FCSTD DOCUMENT  (FreeCAD 1.0R39109 (Git))
Label: AluminumProfiles
License: All rights reserved
LicenseURL: https://en.wikipedia.org/wiki/All_rights_reserved
objects: Sketcher::SketchObject×4
note: 8 computed .brp shape members not serialized (recipe doc carries the construction recipe); baked Part::Feature solids carry a one-line shape summary decoded from their .brp

FEATURE [Sketcher::SketchObject] Sketch  label="2020-4"
  ArcFitTolerance = 1e-06
  FullyConstrained = false
  MakeInternals = false
  sketch-geometry (93):
    g0: LineSegment StartX=7.06065 StartY=6 StartZ=0 EndX=4 EndY=2.93934 EndZ=0
    g1: LineSegment StartX=4 StartY=2.93934 StartZ=0 EndX=4 EndY=2.5 EndZ=0
    g2: LineSegment StartX=4 StartY=2.5 StartZ=0 EndX=3.75098 EndY=1.21889 EndZ=0
    g3: LineSegment StartX=3.75098 StartY=1.21889 StartZ=0 EndX=3.93301 EndY=0.90359 EndZ=0
    g4: ArcOfCircle CenterX=3.5 CenterY=0.65359 CenterZ=0 NormalX=0 NormalY=0 NormalZ=1 AngleXU=0.523601 Radius=0.499998 StartAngle=5.23598 EndAngle=6.28319
    g5: LineSegment StartX=3.93301 StartY=0.40359 StartZ=0 EndX=3.7 EndY=-1e-16 EndZ=0
    g6: LineSegment StartX=3.7 StartY=-1e-16 StartZ=0 EndX=3.93301 EndY=-0.403589 EndZ=0
    g7: ArcOfCircle CenterX=3.5 CenterY=-0.653588 CenterZ=0 NormalX=0 NormalY=0 NormalZ=1 AngleXU=0.523603 Radius=0.499996 StartAngle=5.75958 EndAngle=6.28319
    g8: LineSegment StartX=4 StartY=-0.653589 StartZ=0 EndX=4 EndY=-2.93935 EndZ=0
    g9: LineSegment StartX=4 StartY=-2.93935 StartZ=0 EndX=7.06066 EndY=-6 EndZ=0
    g10: LineSegment StartX=7.06066 StartY=-6 StartZ=0 EndX=8 EndY=-6 EndZ=0
    g11: LineSegment StartX=8 StartY=-6 StartZ=0 EndX=8 EndY=-3.3 EndZ=0
    g12: ArcOfCircle CenterX=8.3 CenterY=-3.3 CenterZ=0 NormalX=0 NormalY=0 NormalZ=1 AngleXU=3.14159 Radius=0.3 StartAngle=4.71239 EndAngle=6.28319
    g13: LineSegment StartX=8.3 StartY=-3 StartZ=0 EndX=9.7 EndY=-3 EndZ=0
    g14: ArcOfCircle CenterX=9.7 CenterY=-3.3 CenterZ=0 NormalX=0 NormalY=0 NormalZ=1 AngleXU=1.5708 Radius=0.3 StartAngle=4.71239 EndAngle=6.28319
    g15: LineSegment StartX=10 StartY=-3.3 StartZ=0 EndX=10 EndY=-9 EndZ=0
    g16: ArcOfCircle CenterX=9 CenterY=-9 CenterZ=0 NormalX=0 NormalY=0 NormalZ=1 AngleXU=3.91e-14 Radius=1 StartAngle=4.71239 EndAngle=6.28319
    g17: LineSegment StartX=9 StartY=-10 StartZ=0 EndX=3.3 EndY=-10 EndZ=0
    g18: ArcOfCircle CenterX=3.3 CenterY=-9.7 CenterZ=0 NormalX=0 NormalY=0 NormalZ=1 AngleXU=-1.5708 Radius=0.3 StartAngle=4.71239 EndAngle=6.28319
    g19: LineSegment StartX=3 StartY=-9.7 StartZ=0 EndX=3 EndY=-8.3 EndZ=0
    g20: ArcOfCircle CenterX=3.3 CenterY=-8.3 CenterZ=0 NormalX=0 NormalY=0 NormalZ=1 AngleXU=3.14159 Radius=0.3 StartAngle=4.71239 EndAngle=6.28319
    g21: LineSegment StartX=3.3 StartY=-8 StartZ=0 EndX=6 EndY=-8 EndZ=0
    g22: LineSegment StartX=6 StartY=-8 StartZ=0 EndX=5.99999 EndY=-7.06066 EndZ=0
    g23: LineSegment StartX=5.99999 StartY=-7.06066 StartZ=0 EndX=2.93932 EndY=-4 EndZ=0
    g24: LineSegment StartX=2.93932 StartY=-4 StartZ=0 EndX=2.5 EndY=-4 EndZ=0
    g25: LineSegment StartX=2.5 StartY=-4 StartZ=0 EndX=1.21889 EndY=-3.75098 EndZ=0
    g26: LineSegment StartX=1.21889 StartY=-3.75098 StartZ=0 EndX=0.90359 EndY=-3.93301 EndZ=0
    g27: ArcOfCircle CenterX=0.65359 CenterY=-3.5 CenterZ=0 NormalX=0 NormalY=0 NormalZ=1 AngleXU=-1.0472 Radius=0.500001 StartAngle=5.23599 EndAngle=6.28319
    g28: LineSegment StartX=0.40359 StartY=-3.93301 StartZ=0 EndX=-1e-16 EndY=-3.7 EndZ=0
    g29: LineSegment StartX=-1e-16 StartY=-3.7 StartZ=0 EndX=-0.403589 EndY=-3.93301 EndZ=0
    g30: ArcOfCircle CenterX=-0.653589 CenterY=-3.5 CenterZ=0 NormalX=0 NormalY=0 NormalZ=1 AngleXU=-1.0472 Radius=0.500002 StartAngle=5.75959 EndAngle=6.28319
    g31: LineSegment StartX=-0.653589 StartY=-4 StartZ=0 EndX=-2.93935 EndY=-4 EndZ=0
    g32: LineSegment StartX=-2.93935 StartY=-4 StartZ=0 EndX=-6 EndY=-7.06066 EndZ=0
    g33: LineSegment StartX=-6 StartY=-7.06066 StartZ=0 EndX=-6 EndY=-8 EndZ=0
    g34: LineSegment StartX=-6 StartY=-8 StartZ=0 EndX=-3.3 EndY=-8 EndZ=0
    g35: ArcOfCircle CenterX=-3.3 CenterY=-8.3 CenterZ=0 NormalX=0 NormalY=0 NormalZ=1 AngleXU=1.5708 Radius=0.3 StartAngle=4.71239 EndAngle=6.28319
    g36: LineSegment StartX=-3 StartY=-8.3 StartZ=0 EndX=-3 EndY=-9.7 EndZ=0
    g37: ArcOfCircle CenterX=-3.3 CenterY=-9.7 CenterZ=0 NormalX=0 NormalY=0 NormalZ=1 AngleXU=1.82496e-07 Radius=0.3 StartAngle=4.71239 EndAngle=6.28319
    g38: ArcOfCircle CenterX=-9 CenterY=-9 CenterZ=0 NormalX=0 NormalY=0 NormalZ=1 AngleXU=-1.5708 Radius=1 StartAngle=4.71239 EndAngle=6.28319
    g39: LineSegment StartX=-10 StartY=-9 StartZ=0 EndX=-10 EndY=-3.3 EndZ=0
    g40: ArcOfCircle CenterX=-9.7 CenterY=-3.3 CenterZ=0 NormalX=0 NormalY=0 NormalZ=1 AngleXU=-3.14159 Radius=0.3 StartAngle=4.71239 EndAngle=6.28319
    g41: LineSegment StartX=-9.7 StartY=-3 StartZ=0 EndX=-8.3 EndY=-3 EndZ=0
    g42: ArcOfCircle CenterX=-8.3 CenterY=-3.3 CenterZ=0 NormalX=0 NormalY=0 NormalZ=1 AngleXU=1.5708 Radius=0.3 StartAngle=4.71239 EndAngle=6.28319
    g43: LineSegment StartX=-8 StartY=-3.3 StartZ=0 EndX=-8 EndY=-6 EndZ=0
    g44: LineSegment StartX=-8 StartY=-6 StartZ=0 EndX=-7.06067 EndY=-6 EndZ=0
    g45: LineSegment StartX=-7.06067 StartY=-6 StartZ=0 EndX=-4 EndY=-2.93934 EndZ=0
    g46: LineSegment StartX=-4 StartY=-2.93934 StartZ=0 EndX=-4 EndY=-2.5 EndZ=0
    g47: LineSegment StartX=-4 StartY=-2.5 StartZ=0 EndX=-3.75098 EndY=-1.21889 EndZ=0
    g48: LineSegment StartX=-3.75098 StartY=-1.21889 StartZ=0 EndX=-3.93301 EndY=-0.903589 EndZ=0
    g49: ArcOfCircle CenterX=-3.5 CenterY=-0.653589 CenterZ=0 NormalX=0 NormalY=0 NormalZ=1 AngleXU=-2.61799 Radius=0.499998 StartAngle=5.23598 EndAngle=6.28319
    g50: LineSegment StartX=-3.93301 StartY=-0.403589 StartZ=0 EndX=-3.7 EndY=0 EndZ=0
    g51: LineSegment StartX=-3.7 StartY=0 StartZ=0 EndX=-3.93301 EndY=0.40359 EndZ=0
    g52: ArcOfCircle CenterX=-3.5 CenterY=0.653589 CenterZ=0 NormalX=0 NormalY=0 NormalZ=1 AngleXU=-2.61799 Radius=0.499996 StartAngle=5.75958 EndAngle=6.28319
    g53: LineSegment StartX=-4 StartY=0.65359 StartZ=0 EndX=-4 EndY=2.93933 EndZ=0
    g54: LineSegment StartX=-4 StartY=2.93933 StartZ=0 EndX=-7.06067 EndY=6 EndZ=0
    g55: LineSegment StartX=-7.06067 StartY=6 StartZ=0 EndX=-8 EndY=6 EndZ=0
    g56: LineSegment StartX=-8 StartY=6 StartZ=0 EndX=-8 EndY=3.3 EndZ=0
    g57: ArcOfCircle CenterX=-8.3 CenterY=3.3 CenterZ=0 NormalX=0 NormalY=0 NormalZ=1 AngleXU=4.74e-14 Radius=0.3 StartAngle=4.71239 EndAngle=6.28319
    g58: LineSegment StartX=-8.3 StartY=3 StartZ=0 EndX=-9.7 EndY=3 EndZ=0
    g59: ArcOfCircle CenterX=-9.7 CenterY=3.3 CenterZ=0 NormalX=0 NormalY=0 NormalZ=1 AngleXU=-1.5708 Radius=0.3 StartAngle=4.71239 EndAngle=6.28319
    g60: LineSegment StartX=-10 StartY=3.3 StartZ=0 EndX=-10 EndY=9 EndZ=0
    g61: ArcOfCircle CenterX=-9 CenterY=9 CenterZ=0 NormalX=0 NormalY=0 NormalZ=1 AngleXU=3.14159 Radius=1 StartAngle=4.71239 EndAngle=6.28319
    g62: LineSegment StartX=-9 StartY=10 StartZ=0 EndX=-3.3 EndY=10 EndZ=0
    g63: ArcOfCircle CenterX=-3.3 CenterY=9.7 CenterZ=0 NormalX=0 NormalY=0 NormalZ=1 AngleXU=1.5708 Radius=0.3 StartAngle=4.71239 EndAngle=6.28319
    g64: LineSegment StartX=-3 StartY=9.7 StartZ=0 EndX=-3 EndY=8.3 EndZ=0
    g65: ArcOfCircle CenterX=-3.3 CenterY=8.3 CenterZ=0 NormalX=0 NormalY=0 NormalZ=1 AngleXU=2.96e-14 Radius=0.3 StartAngle=4.71239 EndAngle=6.28319
    g66: LineSegment StartX=-3.3 StartY=8 StartZ=0 EndX=-6 EndY=8 EndZ=0
    g67: LineSegment StartX=-6 StartY=8 StartZ=0 EndX=-6 EndY=7.06064 EndZ=0
    g68: LineSegment StartX=-6 StartY=7.06064 StartZ=0 EndX=-2.93936 EndY=4 EndZ=0
    g69: LineSegment StartX=-2.93936 StartY=4 StartZ=0 EndX=-2.5 EndY=4 EndZ=0
    g70: LineSegment StartX=-2.5 StartY=4 StartZ=0 EndX=-1.21888 EndY=3.75098 EndZ=0
    g71: LineSegment StartX=-1.21888 StartY=3.75098 StartZ=0 EndX=-0.903589 EndY=3.93301 EndZ=0
    g72: ArcOfCircle CenterX=-0.653589 CenterY=3.5 CenterZ=0 NormalX=0 NormalY=0 NormalZ=1 AngleXU=2.09439 Radius=0.500001 StartAngle=5.23599 EndAngle=6.28319
    g73: LineSegment StartX=-0.403589 StartY=3.93301 StartZ=0 EndX=0 EndY=3.7 EndZ=0
    g74: LineSegment StartX=0 StartY=3.7 StartZ=0 EndX=0.40359 EndY=3.93301 EndZ=0
    g75: ArcOfCircle CenterX=0.65359 CenterY=3.5 CenterZ=0 NormalX=0 NormalY=0 NormalZ=1 AngleXU=2.09439 Radius=0.500002 StartAngle=5.75959 EndAngle=6.28319
    g76: LineSegment StartX=0.65359 StartY=4 StartZ=0 EndX=2.93933 EndY=4 EndZ=0
    g77: LineSegment StartX=2.93933 StartY=4 StartZ=0 EndX=6 EndY=7.06067 EndZ=0
    g78: LineSegment StartX=6 StartY=7.06067 StartZ=0 EndX=6 EndY=8 EndZ=0
    g79: LineSegment StartX=6 StartY=8 StartZ=0 EndX=3.3 EndY=8 EndZ=0
    g80: ArcOfCircle CenterX=3.3 CenterY=8.3 CenterZ=0 NormalX=0 NormalY=0 NormalZ=1 AngleXU=-1.5708 Radius=0.3 StartAngle=4.71239 EndAngle=6.28319
    g81: LineSegment StartX=3 StartY=8.3 StartZ=0 EndX=3 EndY=9.7 EndZ=0
    g82: ArcOfCircle CenterX=3.3 CenterY=9.7 CenterZ=0 NormalX=0 NormalY=0 NormalZ=1 AngleXU=-3.14159 Radius=0.3 StartAngle=4.71239 EndAngle=6.28319
    g83: LineSegment StartX=3.3 StartY=10 StartZ=0 EndX=9 EndY=10 EndZ=0
    g84: ArcOfCircle CenterX=9 CenterY=9 CenterZ=0 NormalX=0 NormalY=0 NormalZ=1 AngleXU=1.5708 Radius=1 StartAngle=4.71239 EndAngle=6.28319
    g85: LineSegment StartX=10 StartY=9 StartZ=0 EndX=10 EndY=3.3 EndZ=0
    g86: ArcOfCircle CenterX=9.7 CenterY=3.3 CenterZ=0 NormalX=0 NormalY=0 NormalZ=1 AngleXU=9.91623e-08 Radius=0.3 StartAngle=4.71239 EndAngle=6.28319
    g87: LineSegment StartX=9.7 StartY=3 StartZ=0 EndX=8.3 EndY=3 EndZ=0
    g88: ArcOfCircle CenterX=8.3 CenterY=3.3 CenterZ=0 NormalX=0 NormalY=0 NormalZ=1 AngleXU=-1.5708 Radius=0.3 StartAngle=4.71239 EndAngle=6.28319
    g89: LineSegment StartX=8 StartY=3.3 StartZ=0 EndX=8 EndY=6 EndZ=0
    g90: LineSegment StartX=8 StartY=6 StartZ=0 EndX=7.06065 EndY=6 EndZ=0
    g91: Circle CenterX=0 CenterY=-2.84e-14 CenterZ=0 NormalX=0 NormalY=0 NormalZ=-1 AngleXU=0 Radius=2.1
    g92: LineSegment StartX=-9 StartY=-10 StartZ=0 EndX=-3.3 EndY=-10 EndZ=0
  constraints (93):
    c: Coincident(g92,g38)
    c: Coincident(g92,g37)
    c: Horizontal(g92)
    c: Coincident(g38,g39)
    c: Coincident(g39,g40)
    c: Coincident(g59,g60)
    c: Coincident(g60,g61)
    c: Coincident(g40,g41)
    c: Coincident(g58,g59)
    c: Coincident(g61,g62)
    c: Coincident(g41,g42)
    c: Coincident(g57,g58)
    c: Coincident(g43,g44)
    c: Coincident(g42,g43)
    c: Coincident(g56,g57)
    c: Coincident(g55,g56)
    c: Coincident(g44,g45)
    c: Coincident(g54,g55)
    c: Coincident(g33,g34)
    c: Coincident(g32,g33)
    c: Coincident(g67,g68)
    c: Coincident(g66,g67)
    c: Coincident(g45,g46)
    c: Coincident(g46,g47)
    c: Coincident(g52,g53)
    c: Coincident(g53,g54)
    c: Coincident(g48,g49)
    c: Coincident(g49,g50)
    c: Coincident(g51,g52)
    c: Coincident(g47,g48)
    c: Coincident(g50,g51)
    c: Coincident(g34,g35)
    c: Coincident(g65,g66)
    c: Coincident(g62,g63)
    c: Coincident(g36,g37)
    c: Coincident(g35,g36)
    c: Coincident(g64,g65)
    c: Coincident(g63,g64)
    c: Coincident(g31,g32)
    c: Coincident(g68,g69)
    c: Coincident(g69,g70)
    c: Coincident(g70,g71)
    c: Coincident(g71,g72)
    c: Coincident(g30,g31)
    c: Coincident(g29,g30)
    c: Coincident(g72,g73)
    c: Coincident(g28,g29)
    c: Coincident(g73,g74)
    c: Coincident(g27,g28)
    c: Coincident(g74,g75)
    c: Coincident(g75,g76)
    c: Coincident(g26,g27)
    c: Coincident(g25,g26)
    c: Coincident(g24,g25)
    c: Coincident(g23,g24)
    c: Coincident(g76,g77)
    c: Coincident(g18,g19)
    c: Coincident(g19,g20)
    c: Coincident(g80,g81)
    c: Coincident(g81,g82)
    c: Coincident(g17,g18)
    c: Coincident(g20,g21)
    c: Coincident(g79,g80)
    c: Coincident(g82,g83)
    c: Coincident(g5,g6)
    c: Coincident(g2,g3)
    c: Coincident(g6,g7)
    c: Coincident(g4,g5)
    c: Coincident(g3,g4)
    c: Coincident(g8,g9)
    c: Coincident(g7,g8)
    c: Coincident(g1,g2)
    c: Coincident(g0,g1)
    c: Coincident(g21,g22)
    c: Coincident(g22,g23)
    c: Coincident(g77,g78)
    c: Coincident(g78,g79)
    c: Coincident(g9,g10)
    c: Coincident(g0,g90)
    c: Coincident(g10,g11)
    c: Coincident(g11,g12)
    c: Coincident(g88,g89)
    c: Coincident(g89,g90)
    c: Coincident(g12,g13)
    c: Coincident(g87,g88)
    c: Coincident(g16,g17)
    c: Coincident(g83,g84)
    c: Coincident(g13,g14)
    c: Coincident(g86,g87)
    c: Coincident(g15,g16)
    c: Coincident(g14,g15)
    c: Coincident(g85,g86)
    c: Coincident(g84,g85)
FEATURE [Sketcher::SketchObject] Sketch001  label="2080-10"
  ArcFitTolerance = 1e-06
  FullyConstrained = false
  MakeInternals = false
  sketch-geometry (287):
    g0: LineSegment StartX=-39 StartY=-10 StartZ=0 EndX=-33.3 EndY=-10 EndZ=0
    g1: ArcOfCircle CenterX=-33.3 CenterY=-9.7 CenterZ=0 NormalX=0 NormalY=0 NormalZ=1 AngleXU=0 Radius=0.3 StartAngle=4.71239 EndAngle=6.28319
    g2: LineSegment StartX=-33 StartY=-9.7 StartZ=0 EndX=-33 EndY=-8.3 EndZ=0
    g3: ArcOfCircle CenterX=-33.3 CenterY=-8.3 CenterZ=0 NormalX=0 NormalY=0 NormalZ=1 AngleXU=0 Radius=0.3 StartAngle=0 EndAngle=1.5708
    g4: LineSegment StartX=-33.3 StartY=-8 StartZ=0 EndX=-36 EndY=-8 EndZ=0
    g5: LineSegment StartX=-36 StartY=-8 StartZ=0 EndX=-36 EndY=-7.06065 EndZ=0
    g6: LineSegment StartX=-36 StartY=-7.06065 StartZ=0 EndX=-32.9394 EndY=-4 EndZ=0
    g7: LineSegment StartX=-32.9394 StartY=-4 StartZ=0 EndX=-30.6536 EndY=-4 EndZ=0
    g8: ArcOfCircle CenterX=-30.6536 CenterY=-3.5 CenterZ=0 NormalX=0 NormalY=0 NormalZ=1 AngleXU=0 Radius=0.500002 StartAngle=4.71239 EndAngle=5.23599
    g9: LineSegment StartX=-30.4036 StartY=-3.93301 StartZ=0 EndX=-30 EndY=-3.7 EndZ=0
    g10: LineSegment StartX=-30 StartY=-3.7 StartZ=0 EndX=-29.5964 EndY=-3.93301 EndZ=0
    g11: ArcOfCircle CenterX=-29.3464 CenterY=-3.5 CenterZ=0 NormalX=0 NormalY=0 NormalZ=1 AngleXU=0 Radius=0.500001 StartAngle=4.18879 EndAngle=5.23599
    g12: LineSegment StartX=-29.0964 StartY=-3.93301 StartZ=0 EndX=-28.7811 EndY=-3.75098 EndZ=0
    g13: LineSegment StartX=-28.7811 StartY=-3.75098 StartZ=0 EndX=-27.5 EndY=-4 EndZ=0
    g14: LineSegment StartX=-27.5 StartY=-4 StartZ=0 EndX=-27.0607 EndY=-4 EndZ=0
    g15: LineSegment StartX=-27.0607 StartY=-4 StartZ=0 EndX=-24 EndY=-7.06068 EndZ=0
    g16: LineSegment StartX=-24 StartY=-7.06068 StartZ=0 EndX=-24 EndY=-8 EndZ=0
    g17: LineSegment StartX=-24 StartY=-8 StartZ=0 EndX=-26.7 EndY=-8 EndZ=0
    g18: ArcOfCircle CenterX=-26.7 CenterY=-8.3 CenterZ=0 NormalX=0 NormalY=0 NormalZ=1 AngleXU=0 Radius=0.3 StartAngle=1.5708 EndAngle=3.14159
    g19: LineSegment StartX=-27 StartY=-8.3 StartZ=0 EndX=-27 EndY=-9.7 EndZ=0
    g20: ArcOfCircle CenterX=-26.7 CenterY=-9.7 CenterZ=0 NormalX=0 NormalY=0 NormalZ=1 AngleXU=0 Radius=0.3 StartAngle=3.14159 EndAngle=4.71239
    g21: LineSegment StartX=-26.7 StartY=-10 StartZ=0 EndX=-13.3 EndY=-10 EndZ=0
    g22: ArcOfCircle CenterX=-13.3 CenterY=-9.7 CenterZ=0 NormalX=0 NormalY=0 NormalZ=1 AngleXU=0 Radius=0.3 StartAngle=4.71239 EndAngle=6.28319
    g23: LineSegment StartX=-13 StartY=-9.7 StartZ=0 EndX=-13 EndY=-8.3 EndZ=0
    g24: ArcOfCircle CenterX=-13.3 CenterY=-8.3 CenterZ=0 NormalX=0 NormalY=0 NormalZ=1 AngleXU=0 Radius=0.3 StartAngle=0 EndAngle=1.5708
    g25: LineSegment StartX=-13.3 StartY=-8 StartZ=0 EndX=-16 EndY=-8 EndZ=0
    g26: LineSegment StartX=-16 StartY=-8 StartZ=0 EndX=-16 EndY=-7.06065 EndZ=0
    g27: LineSegment StartX=-16 StartY=-7.06065 StartZ=0 EndX=-12.9394 EndY=-4 EndZ=0
    g28: LineSegment StartX=-12.9394 StartY=-4 StartZ=0 EndX=-10.6536 EndY=-4 EndZ=0
    g29: ArcOfCircle CenterX=-10.6536 CenterY=-3.5 CenterZ=0 NormalX=0 NormalY=0 NormalZ=1 AngleXU=0 Radius=0.500002 StartAngle=4.71239 EndAngle=5.23599
    g30: LineSegment StartX=-10.4036 StartY=-3.93301 StartZ=0 EndX=-10 EndY=-3.7 EndZ=0
    g31: LineSegment StartX=-10 StartY=-3.7 StartZ=0 EndX=-9.59641 EndY=-3.93301 EndZ=0
    g32: ArcOfCircle CenterX=-9.34641 CenterY=-3.5 CenterZ=0 NormalX=0 NormalY=0 NormalZ=1 AngleXU=0 Radius=0.500001 StartAngle=4.18879 EndAngle=5.23599
    g33: LineSegment StartX=-9.09641 StartY=-3.93301 StartZ=0 EndX=-8.78111 EndY=-3.75098 EndZ=0
    g34: LineSegment StartX=-8.78111 StartY=-3.75098 StartZ=0 EndX=-7.5 EndY=-4 EndZ=0
    g35: LineSegment StartX=-7.5 StartY=-4 StartZ=0 EndX=-7.06067 EndY=-4 EndZ=0
    g36: LineSegment StartX=-7.06067 StartY=-4 StartZ=0 EndX=-4.00001 EndY=-7.06066 EndZ=0
    g37: LineSegment StartX=-4.00001 StartY=-7.06066 StartZ=0 EndX=-4.00001 EndY=-8 EndZ=0
    g38: LineSegment StartX=-4.00001 StartY=-8 StartZ=0 EndX=-6.70001 EndY=-8 EndZ=0
    g39: ArcOfCircle CenterX=-6.70001 CenterY=-8.3 CenterZ=0 NormalX=0 NormalY=0 NormalZ=1 AngleXU=0 Radius=0.3 StartAngle=1.5708 EndAngle=3.14159
    g40: LineSegment StartX=-7.00001 StartY=-8.3 StartZ=0 EndX=-7.00001 EndY=-9.7 EndZ=0
    g41: ArcOfCircle CenterX=-6.70001 CenterY=-9.7 CenterZ=0 NormalX=0 NormalY=0 NormalZ=1 AngleXU=0 Radius=0.3 StartAngle=3.14159 EndAngle=4.71239
    g42: LineSegment StartX=-6.70001 StartY=-10 StartZ=0 EndX=-1.3e-05 EndY=-10 EndZ=0
    g43: LineSegment StartX=-1.3e-05 StartY=-10 StartZ=0 EndX=6.69999 EndY=-10 EndZ=0
    g44: ArcOfCircle CenterX=6.69999 CenterY=-9.7 CenterZ=0 NormalX=0 NormalY=0 NormalZ=1 AngleXU=0 Radius=0.3 StartAngle=4.71239 EndAngle=6.28319
    g45: LineSegment StartX=6.99999 StartY=-9.7 StartZ=0 EndX=6.99999 EndY=-8.3 EndZ=0
    g46: ArcOfCircle CenterX=6.69999 CenterY=-8.3 CenterZ=0 NormalX=0 NormalY=0 NormalZ=1 AngleXU=0 Radius=0.3 StartAngle=0 EndAngle=1.5708
    g47: LineSegment StartX=6.69999 StartY=-8 StartZ=0 EndX=3.99999 EndY=-8 EndZ=0
    g48: LineSegment StartX=3.99999 StartY=-8 StartZ=0 EndX=3.99999 EndY=-7.06065 EndZ=0
    g49: LineSegment StartX=3.99999 StartY=-7.06065 StartZ=0 EndX=7.06064 EndY=-4 EndZ=0
    g50: LineSegment StartX=7.06064 StartY=-4 StartZ=0 EndX=9.34642 EndY=-4 EndZ=0
    g51: ArcOfCircle CenterX=9.34642 CenterY=-3.5 CenterZ=0 NormalX=0 NormalY=0 NormalZ=1 AngleXU=0 Radius=0.500002 StartAngle=4.71239 EndAngle=5.23599
    g52: LineSegment StartX=9.59642 StartY=-3.93301 StartZ=0 EndX=10 EndY=-3.7 EndZ=0
    g53: LineSegment StartX=10 StartY=-3.7 StartZ=0 EndX=10.4036 EndY=-3.93301 EndZ=0
    g54: ArcOfCircle CenterX=10.6536 CenterY=-3.5 CenterZ=0 NormalX=0 NormalY=0 NormalZ=1 AngleXU=0 Radius=0.500001 StartAngle=4.18879 EndAngle=5.23599
    g55: LineSegment StartX=10.9036 StartY=-3.93301 StartZ=0 EndX=11.2189 EndY=-3.75098 EndZ=0
    g56: LineSegment StartX=11.2189 StartY=-3.75098 StartZ=0 EndX=12.5 EndY=-4 EndZ=0
    g57: LineSegment StartX=12.5 StartY=-4 StartZ=0 EndX=12.9393 EndY=-4 EndZ=0
    g58: LineSegment StartX=12.9393 StartY=-4 StartZ=0 EndX=16 EndY=-7.06066 EndZ=0
    g59: LineSegment StartX=16 StartY=-7.06066 StartZ=0 EndX=16 EndY=-8 EndZ=0
    g60: LineSegment StartX=16 StartY=-8 StartZ=0 EndX=13.3 EndY=-8 EndZ=0
    g61: ArcOfCircle CenterX=13.3 CenterY=-8.3 CenterZ=0 NormalX=0 NormalY=0 NormalZ=1 AngleXU=0 Radius=0.3 StartAngle=1.5708 EndAngle=3.14159
    g62: LineSegment StartX=13 StartY=-8.3 StartZ=0 EndX=13 EndY=-9.7 EndZ=0
    g63: ArcOfCircle CenterX=13.3 CenterY=-9.7 CenterZ=0 NormalX=0 NormalY=0 NormalZ=1 AngleXU=0 Radius=0.3 StartAngle=3.14159 EndAngle=4.71239
    g64: LineSegment StartX=13.3 StartY=-10 StartZ=0 EndX=26.7 EndY=-10 EndZ=0
    g65: ArcOfCircle CenterX=26.7 CenterY=-9.7 CenterZ=0 NormalX=0 NormalY=0 NormalZ=1 AngleXU=0 Radius=0.3 StartAngle=4.71239 EndAngle=6.28319
    g66: LineSegment StartX=27 StartY=-9.7 StartZ=0 EndX=27 EndY=-8.3 EndZ=0
    g67: ArcOfCircle CenterX=26.7 CenterY=-8.3 CenterZ=0 NormalX=0 NormalY=0 NormalZ=1 AngleXU=0 Radius=0.3 StartAngle=0 EndAngle=1.5708
    g68: LineSegment StartX=26.7 StartY=-8 StartZ=0 EndX=24 EndY=-8 EndZ=0
    g69: LineSegment StartX=24 StartY=-8 StartZ=0 EndX=24 EndY=-7.06066 EndZ=0
    g70: LineSegment StartX=24 StartY=-7.06066 StartZ=0 EndX=27.0606 EndY=-4 EndZ=0
    g71: LineSegment StartX=27.0606 StartY=-4 StartZ=0 EndX=29.3464 EndY=-4 EndZ=0
    g72: ArcOfCircle CenterX=29.3464 CenterY=-3.5 CenterZ=0 NormalX=0 NormalY=0 NormalZ=1 AngleXU=0 Radius=0.500002 StartAngle=4.71239 EndAngle=5.23599
    g73: LineSegment StartX=29.5964 StartY=-3.93301 StartZ=0 EndX=30 EndY=-3.7 EndZ=0
    g74: LineSegment StartX=30 StartY=-3.7 StartZ=0 EndX=30.4036 EndY=-3.93301 EndZ=0
    g75: ArcOfCircle CenterX=30.6536 CenterY=-3.5 CenterZ=0 NormalX=0 NormalY=0 NormalZ=1 AngleXU=0 Radius=0.500001 StartAngle=4.18879 EndAngle=5.23599
    g76: LineSegment StartX=30.9036 StartY=-3.93301 StartZ=0 EndX=31.2189 EndY=-3.75098 EndZ=0
    g77: LineSegment StartX=31.2189 StartY=-3.75098 StartZ=0 EndX=32.5 EndY=-4 EndZ=0
    g78: LineSegment StartX=32.5 StartY=-4 StartZ=0 EndX=32.9393 EndY=-4 EndZ=0
    g79: LineSegment StartX=32.9393 StartY=-4 StartZ=0 EndX=36 EndY=-7.06064 EndZ=0
    g80: LineSegment StartX=36 StartY=-7.06064 StartZ=0 EndX=36 EndY=-8 EndZ=0
    g81: LineSegment StartX=36 StartY=-8 StartZ=0 EndX=33.3 EndY=-8 EndZ=0
    g82: ArcOfCircle CenterX=33.3 CenterY=-8.3 CenterZ=0 NormalX=0 NormalY=0 NormalZ=1 AngleXU=0 Radius=0.3 StartAngle=1.5708 EndAngle=3.14159
    g83: LineSegment StartX=33 StartY=-8.3 StartZ=0 EndX=33 EndY=-9.7 EndZ=0
    g84: ArcOfCircle CenterX=33.3 CenterY=-9.7 CenterZ=0 NormalX=0 NormalY=0 NormalZ=1 AngleXU=0 Radius=0.3 StartAngle=3.14159 EndAngle=4.71239
    g85: LineSegment StartX=33.3 StartY=-10 StartZ=0 EndX=39 EndY=-10 EndZ=0
    g86: ArcOfCircle CenterX=39 CenterY=-9 CenterZ=0 NormalX=0 NormalY=0 NormalZ=1 AngleXU=0 Radius=1 StartAngle=4.71239 EndAngle=6.28319
    g87: LineSegment StartX=40 StartY=-9 StartZ=0 EndX=40 EndY=-3.3 EndZ=0
    g88: ArcOfCircle CenterX=39.7 CenterY=-3.3 CenterZ=0 NormalX=0 NormalY=0 NormalZ=1 AngleXU=0 Radius=0.3 StartAngle=0 EndAngle=1.5708
    g89: LineSegment StartX=39.7 StartY=-3 StartZ=0 EndX=38.3 EndY=-3 EndZ=0
    g90: ArcOfCircle CenterX=38.3 CenterY=-3.3 CenterZ=0 NormalX=0 NormalY=0 NormalZ=1 AngleXU=0 Radius=0.3 StartAngle=1.5708 EndAngle=3.14159
    g91: LineSegment StartX=38 StartY=-3.3 StartZ=0 EndX=38 EndY=-6 EndZ=0
    g92: LineSegment StartX=38 StartY=-6 StartZ=0 EndX=37.0607 EndY=-6 EndZ=0
    g93: LineSegment StartX=37.0607 StartY=-6 StartZ=0 EndX=34 EndY=-2.93932 EndZ=0
    g94: LineSegment StartX=34 StartY=-2.93932 StartZ=0 EndX=34 EndY=-0.653589 EndZ=0
    g95: ArcOfCircle CenterX=33.5 CenterY=-0.653589 CenterZ=0 NormalX=0 NormalY=0 NormalZ=1 AngleXU=0 Radius=0.499996 StartAngle=6.28318 EndAngle=6.80679
    g96: LineSegment StartX=33.933 StartY=-0.403589 StartZ=0 EndX=33.7 EndY=0 EndZ=0
    g97: LineSegment StartX=33.7 StartY=0 StartZ=0 EndX=33.933 EndY=0.403589 EndZ=0
    g98: ArcOfCircle CenterX=33.5 CenterY=0.653589 CenterZ=0 NormalX=0 NormalY=0 NormalZ=1 AngleXU=0 Radius=0.499998 StartAngle=5.75958 EndAngle=6.80679
    g99: LineSegment StartX=33.933 StartY=0.903589 StartZ=0 EndX=33.751 EndY=1.21889 EndZ=0
    g100: LineSegment StartX=33.751 StartY=1.21889 StartZ=0 EndX=34 EndY=2.5 EndZ=0
    g101: LineSegment StartX=34 StartY=2.5 StartZ=0 EndX=34 EndY=2.93932 EndZ=0
    g102: LineSegment StartX=34 StartY=2.93932 StartZ=0 EndX=37.0607 EndY=6 EndZ=0
    g103: LineSegment StartX=37.0607 StartY=6 StartZ=0 EndX=38 EndY=6 EndZ=0
    g104: LineSegment StartX=38 StartY=6 StartZ=0 EndX=38 EndY=3.3 EndZ=0
    g105: ArcOfCircle CenterX=38.3 CenterY=3.3 CenterZ=0 NormalX=0 NormalY=0 NormalZ=1 AngleXU=0 Radius=0.3 StartAngle=3.14159 EndAngle=4.71239
    g106: LineSegment StartX=38.3 StartY=3 StartZ=0 EndX=39.7 EndY=3 EndZ=0
    g107: ArcOfCircle CenterX=39.7 CenterY=3.3 CenterZ=0 NormalX=0 NormalY=0 NormalZ=1 AngleXU=0 Radius=0.3 StartAngle=4.71239 EndAngle=6.28319
    g108: LineSegment StartX=40 StartY=3.3 StartZ=0 EndX=40 EndY=9 EndZ=0
    g109: ArcOfCircle CenterX=39 CenterY=9 CenterZ=0 NormalX=0 NormalY=0 NormalZ=1 AngleXU=0 Radius=1 StartAngle=6.28319 EndAngle=7.85398
    g110: LineSegment StartX=39 StartY=10 StartZ=0 EndX=33.3 EndY=10 EndZ=0
    g111: ArcOfCircle CenterX=33.3 CenterY=9.7 CenterZ=0 NormalX=0 NormalY=0 NormalZ=1 AngleXU=0 Radius=0.3 StartAngle=1.5708 EndAngle=3.14159
    g112: LineSegment StartX=33 StartY=9.7 StartZ=0 EndX=33 EndY=8.3 EndZ=0
    g113: ArcOfCircle CenterX=33.3 CenterY=8.3 CenterZ=0 NormalX=0 NormalY=0 NormalZ=1 AngleXU=0 Radius=0.3 StartAngle=3.14159 EndAngle=4.71239
    g114: LineSegment StartX=33.3 StartY=8 StartZ=0 EndX=36 EndY=8 EndZ=0
    g115: LineSegment StartX=36 StartY=8 StartZ=0 EndX=36 EndY=7.06064 EndZ=0
    g116: LineSegment StartX=36 StartY=7.06064 StartZ=0 EndX=32.9393 EndY=4 EndZ=0
    g117: LineSegment StartX=32.9393 StartY=4 StartZ=0 EndX=30.6536 EndY=4 EndZ=0
    g118: ArcOfCircle CenterX=30.6536 CenterY=3.5 CenterZ=0 NormalX=0 NormalY=0 NormalZ=1 AngleXU=0 Radius=0.500002 StartAngle=1.5708 EndAngle=2.09439
    g119: LineSegment StartX=30.4036 StartY=3.93301 StartZ=0 EndX=30 EndY=3.7 EndZ=0
    g120: LineSegment StartX=30 StartY=3.7 StartZ=0 EndX=29.5964 EndY=3.93301 EndZ=0
    g121: ArcOfCircle CenterX=29.3464 CenterY=3.5 CenterZ=0 NormalX=0 NormalY=0 NormalZ=1 AngleXU=0 Radius=0.500001 StartAngle=1.0472 EndAngle=2.09439
    g122: LineSegment StartX=29.0964 StartY=3.93301 StartZ=0 EndX=28.7811 EndY=3.75098 EndZ=0
    g123: LineSegment StartX=28.7811 StartY=3.75098 StartZ=0 EndX=27.5 EndY=4 EndZ=0
    g124: LineSegment StartX=27.5 StartY=4 StartZ=0 EndX=27.0607 EndY=4 EndZ=0
    g125: LineSegment StartX=27.0607 StartY=4 StartZ=0 EndX=24 EndY=7.06067 EndZ=0
    g126: LineSegment StartX=24 StartY=7.06067 StartZ=0 EndX=24 EndY=8 EndZ=0
    g127: LineSegment StartX=24 StartY=8 StartZ=0 EndX=26.7 EndY=8 EndZ=0
    g128: ArcOfCircle CenterX=26.7 CenterY=8.3 CenterZ=0 NormalX=0 NormalY=0 NormalZ=1 AngleXU=0 Radius=0.3 StartAngle=4.71239 EndAngle=6.28319
    g129: LineSegment StartX=27 StartY=8.3 StartZ=0 EndX=27 EndY=9.7 EndZ=0
    g130: ArcOfCircle CenterX=26.7 CenterY=9.7 CenterZ=0 NormalX=0 NormalY=0 NormalZ=1 AngleXU=0 Radius=0.3 StartAngle=0 EndAngle=1.5708
    g131: LineSegment StartX=26.7 StartY=10 StartZ=0 EndX=13.3 EndY=10 EndZ=0
    g132: ArcOfCircle CenterX=13.3 CenterY=9.7 CenterZ=0 NormalX=0 NormalY=0 NormalZ=1 AngleXU=0 Radius=0.3 StartAngle=1.5708 EndAngle=3.14159
    g133: LineSegment StartX=13 StartY=9.7 StartZ=0 EndX=13 EndY=8.3 EndZ=0
    g134: ArcOfCircle CenterX=13.3 CenterY=8.3 CenterZ=0 NormalX=0 NormalY=0 NormalZ=1 AngleXU=0 Radius=0.3 StartAngle=3.14159 EndAngle=4.71239
    g135: LineSegment StartX=13.3 StartY=8 StartZ=0 EndX=16 EndY=8 EndZ=0
    g136: LineSegment StartX=16 StartY=8 StartZ=0 EndX=16 EndY=7.06065 EndZ=0
    g137: LineSegment StartX=16 StartY=7.06065 StartZ=0 EndX=12.9393 EndY=4 EndZ=0
    g138: LineSegment StartX=12.9393 StartY=4 StartZ=0 EndX=10.6536 EndY=4 EndZ=0
    g139: ArcOfCircle CenterX=10.6536 CenterY=3.5 CenterZ=0 NormalX=0 NormalY=0 NormalZ=1 AngleXU=0 Radius=0.500002 StartAngle=1.5708 EndAngle=2.09439
    g140: LineSegment StartX=10.4036 StartY=3.93301 StartZ=0 EndX=10 EndY=3.7 EndZ=0
    g141: LineSegment StartX=10 StartY=3.7 StartZ=0 EndX=9.59641 EndY=3.93301 EndZ=0
    g142: ArcOfCircle CenterX=9.34642 CenterY=3.5 CenterZ=0 NormalX=0 NormalY=0 NormalZ=1 AngleXU=0 Radius=0.500001 StartAngle=1.0472 EndAngle=2.09439
    g143: LineSegment StartX=9.09641 StartY=3.93301 StartZ=0 EndX=8.78112 EndY=3.75098 EndZ=0
    g144: LineSegment StartX=8.78112 StartY=3.75098 StartZ=0 EndX=7.5 EndY=4 EndZ=0
    g145: LineSegment StartX=7.5 StartY=4 StartZ=0 EndX=7.06064 EndY=4 EndZ=0
    g146: LineSegment StartX=7.06064 StartY=4 StartZ=0 EndX=3.99999 EndY=7.06065 EndZ=0
    g147: LineSegment StartX=3.99999 StartY=7.06065 StartZ=0 EndX=3.99999 EndY=8 EndZ=0
    g148: LineSegment StartX=3.99999 StartY=8 StartZ=0 EndX=6.69999 EndY=8 EndZ=0
    g149: ArcOfCircle CenterX=6.69999 CenterY=8.3 CenterZ=0 NormalX=0 NormalY=0 NormalZ=1 AngleXU=0 Radius=0.3 StartAngle=4.71239 EndAngle=6.28319
    g150: LineSegment StartX=6.99999 StartY=8.3 StartZ=0 EndX=6.99999 EndY=9.7 EndZ=0
    g151: ArcOfCircle CenterX=6.69999 CenterY=9.7 CenterZ=0 NormalX=0 NormalY=0 NormalZ=1 AngleXU=0 Radius=0.3 StartAngle=0 EndAngle=1.5708
    g152: LineSegment StartX=6.69999 StartY=10 StartZ=0 EndX=-1.3e-05 EndY=10 EndZ=0
    g153: LineSegment StartX=-1.3e-05 StartY=10 StartZ=0 EndX=-6.70001 EndY=10 EndZ=0
    g154: ArcOfCircle CenterX=-6.70001 CenterY=9.7 CenterZ=0 NormalX=0 NormalY=0 NormalZ=1 AngleXU=0 Radius=0.3 StartAngle=1.5708 EndAngle=3.14159
    g155: LineSegment StartX=-7.00001 StartY=9.7 StartZ=0 EndX=-7.00001 EndY=8.3 EndZ=0
    g156: ArcOfCircle CenterX=-6.70001 CenterY=8.3 CenterZ=0 NormalX=0 NormalY=0 NormalZ=1 AngleXU=0 Radius=0.3 StartAngle=3.14159 EndAngle=4.71239
    g157: LineSegment StartX=-6.70001 StartY=8 StartZ=0 EndX=-4.00001 EndY=8 EndZ=0
    g158: LineSegment StartX=-4.00001 StartY=8 StartZ=0 EndX=-4.00001 EndY=7.06065 EndZ=0
    g159: LineSegment StartX=-4.00001 StartY=7.06065 StartZ=0 EndX=-7.06066 EndY=4 EndZ=0
    g160: LineSegment StartX=-7.06066 StartY=4 StartZ=0 EndX=-9.34641 EndY=4 EndZ=0
    g161: ArcOfCircle CenterX=-9.34641 CenterY=3.5 CenterZ=0 NormalX=0 NormalY=0 NormalZ=1 AngleXU=0 Radius=0.500002 StartAngle=1.5708 EndAngle=2.09439
    g162: LineSegment StartX=-9.59641 StartY=3.93301 StartZ=0 EndX=-10 EndY=3.7 EndZ=0
    g163: LineSegment StartX=-10 StartY=3.7 StartZ=0 EndX=-10.4036 EndY=3.93301 EndZ=0
    g164: ArcOfCircle CenterX=-10.6536 CenterY=3.5 CenterZ=0 NormalX=0 NormalY=0 NormalZ=1 AngleXU=0 Radius=0.500001 StartAngle=1.0472 EndAngle=2.09439
    g165: LineSegment StartX=-10.9036 StartY=3.93301 StartZ=0 EndX=-11.2189 EndY=3.75098 EndZ=0
    g166: LineSegment StartX=-11.2189 StartY=3.75098 StartZ=0 EndX=-12.5 EndY=4 EndZ=0
    g167: LineSegment StartX=-12.5 StartY=4 StartZ=0 EndX=-12.9394 EndY=4 EndZ=0
    g168: LineSegment StartX=-12.9394 StartY=4 StartZ=0 EndX=-16 EndY=7.06065 EndZ=0
    g169: LineSegment StartX=-16 StartY=7.06065 StartZ=0 EndX=-16 EndY=8 EndZ=0
    g170: LineSegment StartX=-16 StartY=8 StartZ=0 EndX=-13.3 EndY=8 EndZ=0
    g171: ArcOfCircle CenterX=-13.3 CenterY=8.3 CenterZ=0 NormalX=0 NormalY=0 NormalZ=1 AngleXU=0 Radius=0.3 StartAngle=4.71239 EndAngle=6.28319
    g172: LineSegment StartX=-13 StartY=8.3 StartZ=0 EndX=-13 EndY=9.7 EndZ=0
    g173: ArcOfCircle CenterX=-13.3 CenterY=9.7 CenterZ=0 NormalX=0 NormalY=0 NormalZ=1 AngleXU=0 Radius=0.3 StartAngle=0 EndAngle=1.5708
    g174: LineSegment StartX=-13.3 StartY=10 StartZ=0 EndX=-26.7 EndY=10 EndZ=0
    g175: ArcOfCircle CenterX=-26.7 CenterY=9.7 CenterZ=0 NormalX=0 NormalY=0 NormalZ=1 AngleXU=0 Radius=0.3 StartAngle=1.5708 EndAngle=3.14159
    g176: LineSegment StartX=-27 StartY=9.7 StartZ=0 EndX=-27 EndY=8.3 EndZ=0
    g177: ArcOfCircle CenterX=-26.7 CenterY=8.3 CenterZ=0 NormalX=0 NormalY=0 NormalZ=1 AngleXU=0 Radius=0.3 StartAngle=3.14159 EndAngle=4.71239
    g178: LineSegment StartX=-26.7 StartY=8 StartZ=0 EndX=-24 EndY=8 EndZ=0
    g179: LineSegment StartX=-24 StartY=8 StartZ=0 EndX=-24 EndY=7.06067 EndZ=0
    g180: LineSegment StartX=-24 StartY=7.06067 StartZ=0 EndX=-27.0607 EndY=4 EndZ=0
    g181: LineSegment StartX=-27.0607 StartY=4 StartZ=0 EndX=-29.3464 EndY=4 EndZ=0
    g182: ArcOfCircle CenterX=-29.3464 CenterY=3.5 CenterZ=0 NormalX=0 NormalY=0 NormalZ=1 AngleXU=0 Radius=0.500002 StartAngle=1.5708 EndAngle=2.09439
    g183: LineSegment StartX=-29.5964 StartY=3.93301 StartZ=0 EndX=-30 EndY=3.7 EndZ=0
    g184: LineSegment StartX=-30 StartY=3.7 StartZ=0 EndX=-30.4036 EndY=3.93301 EndZ=0
    g185: ArcOfCircle CenterX=-30.6536 CenterY=3.5 CenterZ=0 NormalX=0 NormalY=0 NormalZ=1 AngleXU=0 Radius=0.500001 StartAngle=1.0472 EndAngle=2.09439
    g186: LineSegment StartX=-30.9036 StartY=3.93301 StartZ=0 EndX=-31.2189 EndY=3.75098 EndZ=0
    g187: LineSegment StartX=-31.2189 StartY=3.75098 StartZ=0 EndX=-32.5 EndY=4 EndZ=0
    g188: LineSegment StartX=-32.5 StartY=4 StartZ=0 EndX=-32.9394 EndY=4 EndZ=0
    g189: LineSegment StartX=-32.9394 StartY=4 StartZ=0 EndX=-36 EndY=7.06064 EndZ=0
    g190: LineSegment StartX=-36 StartY=7.06064 StartZ=0 EndX=-36 EndY=8 EndZ=0
    g191: LineSegment StartX=-36 StartY=8 StartZ=0 EndX=-33.3 EndY=8 EndZ=0
    g192: ArcOfCircle CenterX=-33.3 CenterY=8.3 CenterZ=0 NormalX=0 NormalY=0 NormalZ=1 AngleXU=0 Radius=0.3 StartAngle=4.71239 EndAngle=6.28319
    g193: LineSegment StartX=-33 StartY=8.3 StartZ=0 EndX=-33 EndY=9.7 EndZ=0
    g194: ArcOfCircle CenterX=-33.3 CenterY=9.7 CenterZ=0 NormalX=0 NormalY=0 NormalZ=1 AngleXU=0 Radius=0.3 StartAngle=0 EndAngle=1.5708
    g195: LineSegment StartX=-33.3 StartY=10 StartZ=0 EndX=-39 EndY=10 EndZ=0
    g196: ArcOfCircle CenterX=-39 CenterY=9 CenterZ=0 NormalX=0 NormalY=0 NormalZ=1 AngleXU=0 Radius=1 StartAngle=1.5708 EndAngle=3.14159
    g197: LineSegment StartX=-40 StartY=9 StartZ=0 EndX=-40 EndY=3.3 EndZ=0
    g198: ArcOfCircle CenterX=-39.7 CenterY=3.3 CenterZ=0 NormalX=0 NormalY=0 NormalZ=1 AngleXU=0 Radius=0.3 StartAngle=3.14159 EndAngle=4.71239
    g199: LineSegment StartX=-39.7 StartY=3 StartZ=0 EndX=-38.3 EndY=3 EndZ=0
    g200: ArcOfCircle CenterX=-38.3 CenterY=3.3 CenterZ=0 NormalX=0 NormalY=0 NormalZ=1 AngleXU=0 Radius=0.3 StartAngle=4.71239 EndAngle=6.28319
    g201: LineSegment StartX=-38 StartY=3.3 StartZ=0 EndX=-38 EndY=6 EndZ=0
    g202: LineSegment StartX=-38 StartY=6 StartZ=0 EndX=-37.0607 EndY=6 EndZ=0
    g203: LineSegment StartX=-37.0607 StartY=6 StartZ=0 EndX=-34 EndY=2.93933 EndZ=0
    g204: LineSegment StartX=-34 StartY=2.93933 StartZ=0 EndX=-34 EndY=0.65359 EndZ=0
    g205: ArcOfCircle CenterX=-33.5 CenterY=0.653589 CenterZ=0 NormalX=0 NormalY=0 NormalZ=1 AngleXU=0 Radius=0.499996 StartAngle=3.14159 EndAngle=3.6652
    g206: LineSegment StartX=-33.933 StartY=0.403589 StartZ=0 EndX=-33.7 EndY=0 EndZ=0
    g207: LineSegment StartX=-33.7 StartY=0 StartZ=0 EndX=-33.933 EndY=-0.403589 EndZ=0
    g208: ArcOfCircle CenterX=-33.5 CenterY=-0.653589 CenterZ=0 NormalX=0 NormalY=0 NormalZ=1 AngleXU=0 Radius=0.499998 StartAngle=2.61799 EndAngle=3.66519
    g209: LineSegment StartX=-33.933 StartY=-0.903589 StartZ=0 EndX=-33.751 EndY=-1.21889 EndZ=0
    g210: LineSegment StartX=-33.751 StartY=-1.21889 StartZ=0 EndX=-34 EndY=-2.5 EndZ=0
    g211: LineSegment StartX=-34 StartY=-2.5 StartZ=0 EndX=-34 EndY=-2.93934 EndZ=0
    g212: LineSegment StartX=-34 StartY=-2.93934 StartZ=0 EndX=-37.0607 EndY=-6 EndZ=0
    g213: LineSegment StartX=-37.0607 StartY=-6 StartZ=0 EndX=-38 EndY=-6 EndZ=0
    g214: LineSegment StartX=-38 StartY=-6 StartZ=0 EndX=-38 EndY=-3.3 EndZ=0
    g215: ArcOfCircle CenterX=-38.3 CenterY=-3.3 CenterZ=0 NormalX=0 NormalY=0 NormalZ=1 AngleXU=0 Radius=0.3 StartAngle=0 EndAngle=1.5708
    g216: LineSegment StartX=-38.3 StartY=-3 StartZ=0 EndX=-39.7 EndY=-3 EndZ=0
    g217: ArcOfCircle CenterX=-39.7 CenterY=-3.3 CenterZ=0 NormalX=0 NormalY=0 NormalZ=1 AngleXU=0 Radius=0.3 StartAngle=1.5708 EndAngle=3.14159
    g218: LineSegment StartX=-40 StartY=-3.3 StartZ=0 EndX=-40 EndY=-9 EndZ=0
    g219: ArcOfCircle CenterX=-39 CenterY=-9 CenterZ=0 NormalX=0 NormalY=0 NormalZ=1 AngleXU=0 Radius=1 StartAngle=3.14159 EndAngle=4.71239
    g220: ArcOfCircle CenterX=-22.3 CenterY=-7.0636 CenterZ=0 NormalX=0 NormalY=0 NormalZ=1 AngleXU=0 Radius=0.3 StartAngle=6.28318 EndAngle=7.06858
    g221: LineSegment StartX=-22.0902 StartY=-6.84915 StartZ=0 EndX=-22.0879 EndY=-6.85146 EndZ=0
    g222: LineSegment StartX=-26 StartY=-2.93935 StartZ=0 EndX=-22.0902 EndY=-6.84915 EndZ=0
    g223: LineSegment StartX=-26 StartY=2.93934 StartZ=0 EndX=-26 EndY=-2.93935 EndZ=0
    g224: LineSegment StartX=-22.0879 StartY=6.85148 StartZ=0 EndX=-26 EndY=2.93934 EndZ=0
    g225: ArcOfCircle CenterX=-22.3 CenterY=7.06362 CenterZ=0 NormalX=0 NormalY=0 NormalZ=1 AngleXU=0 Radius=0.3 StartAngle=5.49779 EndAngle=6.28318
    g226: LineSegment StartX=-22 StartY=7.7 StartZ=0 EndX=-22 EndY=7.06362 EndZ=0
    g227: ArcOfCircle CenterX=-21.7 CenterY=7.7 CenterZ=0 NormalX=0 NormalY=0 NormalZ=1 AngleXU=0 Radius=0.3 StartAngle=1.5708 EndAngle=3.14159
    g228: LineSegment StartX=-18.3 StartY=8 StartZ=0 EndX=-21.7 EndY=8 EndZ=0
    g229: ArcOfCircle CenterX=-18.3 CenterY=7.7 CenterZ=0 NormalX=0 NormalY=0 NormalZ=1 AngleXU=0 Radius=0.3 StartAngle=0 EndAngle=1.5708
    g230: LineSegment StartX=-18 StartY=7.06359 StartZ=0 EndX=-18 EndY=7.7 EndZ=0
    g231: ArcOfCircle CenterX=-17.7 CenterY=7.06359 CenterZ=0 NormalX=0 NormalY=0 NormalZ=1 AngleXU=0 Radius=0.3 StartAngle=3.14159 EndAngle=3.92699
    g232: LineSegment StartX=-14 StartY=2.93933 StartZ=0 EndX=-17.9121 EndY=6.85146 EndZ=0
    g233: LineSegment StartX=-14 StartY=-2.93933 StartZ=0 EndX=-14 EndY=2.93933 EndZ=0
    g234: LineSegment StartX=-17.9121 StartY=-6.85146 StartZ=0 EndX=-14 EndY=-2.93933 EndZ=0
    g235: ArcOfCircle CenterX=-17.7 CenterY=-7.0636 CenterZ=0 NormalX=0 NormalY=0 NormalZ=1 AngleXU=0 Radius=0.3 StartAngle=2.35619 EndAngle=3.14159
    g236: LineSegment StartX=-18 StartY=-7.7 StartZ=0 EndX=-18 EndY=-7.0636 EndZ=0
    g237: ArcOfCircle CenterX=-18.3 CenterY=-7.7 CenterZ=0 NormalX=0 NormalY=0 NormalZ=1 AngleXU=0 Radius=0.3 StartAngle=4.71239 EndAngle=6.28319
    g238: LineSegment StartX=-21.7 StartY=-8 StartZ=0 EndX=-18.3 EndY=-8 EndZ=0
    g239: ArcOfCircle CenterX=-21.7 CenterY=-7.7 CenterZ=0 NormalX=0 NormalY=0 NormalZ=1 AngleXU=0 Radius=0.3 StartAngle=3.14159 EndAngle=4.71239
    g240: LineSegment StartX=-22 StartY=-7.0636 StartZ=0 EndX=-22 EndY=-7.7 EndZ=0
    g241: Circle CenterX=-30 CenterY=0 CenterZ=0 NormalX=0 NormalY=0 NormalZ=-1 AngleXU=0 Radius=2.1
    g242: Circle CenterX=-10 CenterY=0 CenterZ=0 NormalX=0 NormalY=0 NormalZ=-1 AngleXU=0 Radius=2.1
    g243: LineSegment StartX=-1.70001 StartY=-8 StartZ=0 EndX=-1.3e-05 EndY=-8 EndZ=0
    g244: ArcOfCircle CenterX=-1.70001 CenterY=-7.7 CenterZ=0 NormalX=0 NormalY=0 NormalZ=1 AngleXU=0 Radius=0.3 StartAngle=3.14159 EndAngle=4.71239
    g245: LineSegment StartX=-2.00001 StartY=-7.0636 StartZ=0 EndX=-2.00001 EndY=-7.7 EndZ=0
    g246: ArcOfCircle CenterX=-2.30001 CenterY=-7.0636 CenterZ=0 NormalX=0 NormalY=0 NormalZ=1 AngleXU=0 Radius=0.3 StartAngle=6.28318 EndAngle=7.06858
    g247: LineSegment StartX=-6.00001 StartY=-2.93934 StartZ=0 EndX=-2.08788 EndY=-6.85147 EndZ=0
    g248: LineSegment StartX=-6.00001 StartY=2.93933 StartZ=0 EndX=-6.00001 EndY=-2.93934 EndZ=0
    g249: LineSegment StartX=-2.08788 StartY=6.85146 StartZ=0 EndX=-6.00001 EndY=2.93933 EndZ=0
    g250: ArcOfCircle CenterX=-2.30001 CenterY=7.06359 CenterZ=0 NormalX=0 NormalY=0 NormalZ=1 AngleXU=0 Radius=0.3 StartAngle=5.49779 EndAngle=6.28318
    g251: LineSegment StartX=-2.00001 StartY=7.7 StartZ=0 EndX=-2.00001 EndY=7.06359 EndZ=0
    g252: ArcOfCircle CenterX=-1.70001 CenterY=7.7 CenterZ=0 NormalX=0 NormalY=0 NormalZ=1 AngleXU=0 Radius=0.3 StartAngle=1.5708 EndAngle=3.14159
    g253: LineSegment StartX=-1.3e-05 StartY=8 StartZ=0 EndX=-1.70001 EndY=8 EndZ=0
    g254: LineSegment StartX=1.69999 StartY=8 StartZ=0 EndX=-1.3e-05 EndY=8 EndZ=0
    g255: ArcOfCircle CenterX=1.69999 CenterY=7.7 CenterZ=0 NormalX=0 NormalY=0 NormalZ=1 AngleXU=0 Radius=0.3 StartAngle=0 EndAngle=1.5708
    g256: LineSegment StartX=1.99999 StartY=7.06359 StartZ=0 EndX=1.99999 EndY=7.7 EndZ=0
    g257: ArcOfCircle CenterX=2.29999 CenterY=7.06359 CenterZ=0 NormalX=0 NormalY=0 NormalZ=1 AngleXU=0 Radius=0.3 StartAngle=3.14159 EndAngle=3.92699
    g258: LineSegment StartX=5.99999 StartY=2.93933 StartZ=0 EndX=2.08786 EndY=6.85146 EndZ=0
    g259: LineSegment StartX=5.99998 StartY=-2.93933 StartZ=0 EndX=5.99999 EndY=2.93933 EndZ=0
    g260: LineSegment StartX=2.08786 StartY=-6.85146 StartZ=0 EndX=5.99998 EndY=-2.93933 EndZ=0
    g261: ArcOfCircle CenterX=2.29999 CenterY=-7.0636 CenterZ=0 NormalX=0 NormalY=0 NormalZ=1 AngleXU=0 Radius=0.3 StartAngle=2.35619 EndAngle=3.14159
    g262: LineSegment StartX=1.99999 StartY=-7.7 StartZ=0 EndX=1.99999 EndY=-7.0636 EndZ=0
    g263: ArcOfCircle CenterX=1.69999 CenterY=-7.7 CenterZ=0 NormalX=0 NormalY=0 NormalZ=1 AngleXU=0 Radius=0.3 StartAngle=4.71239 EndAngle=6.28319
    g264: LineSegment StartX=-1.3e-05 StartY=-8 StartZ=0 EndX=1.69999 EndY=-8 EndZ=0
    g265: Circle CenterX=9.99999 CenterY=0 CenterZ=0 NormalX=0 NormalY=0 NormalZ=-1 AngleXU=0 Radius=2.1
    g266: LineSegment StartX=26 StartY=2.93935 StartZ=0 EndX=22.0879 EndY=6.85148 EndZ=0
    g267: LineSegment StartX=26 StartY=2.93935 StartZ=0 EndX=26 EndY=-2.93934 EndZ=0
    g268: LineSegment StartX=22.0879 StartY=-6.85147 StartZ=0 EndX=26 EndY=-2.93934 EndZ=0
    g269: ArcOfCircle CenterX=22.3 CenterY=-7.0636 CenterZ=0 NormalX=0 NormalY=0 NormalZ=1 AngleXU=0 Radius=0.3 StartAngle=2.35619 EndAngle=3.14159
    g270: LineSegment StartX=22 StartY=-7.0636 StartZ=0 EndX=22 EndY=-7.7 EndZ=0
    g271: ArcOfCircle CenterX=21.7 CenterY=-7.7 CenterZ=0 NormalX=0 NormalY=0 NormalZ=1 AngleXU=0 Radius=0.3 StartAngle=4.71239 EndAngle=6.28318
    g272: LineSegment StartX=18.3 StartY=-8 StartZ=0 EndX=21.7 EndY=-8 EndZ=0
    g273: ArcOfCircle CenterX=18.3 CenterY=-7.7 CenterZ=0 NormalX=0 NormalY=0 NormalZ=1 AngleXU=0 Radius=0.3 StartAngle=3.14159 EndAngle=4.71239
    g274: LineSegment StartX=18 StartY=-7.0636 StartZ=0 EndX=18 EndY=-7.7 EndZ=0
    g275: ArcOfCircle CenterX=17.7 CenterY=-7.0636 CenterZ=0 NormalX=0 NormalY=0 NormalZ=1 AngleXU=0 Radius=0.3 StartAngle=0 EndAngle=0.785398
    g276: LineSegment StartX=14 StartY=-2.93934 StartZ=0 EndX=17.9121 EndY=-6.85147 EndZ=0
    g277: LineSegment StartX=14 StartY=2.93933 StartZ=0 EndX=14 EndY=-2.93934 EndZ=0
    g278: LineSegment StartX=17.9121 StartY=6.85146 StartZ=0 EndX=14 EndY=2.93933 EndZ=0
    g279: ArcOfCircle CenterX=17.7 CenterY=7.06359 CenterZ=0 NormalX=0 NormalY=0 NormalZ=1 AngleXU=0 Radius=0.3 StartAngle=5.49779 EndAngle=6.28318
    g280: LineSegment StartX=18 StartY=7.7 StartZ=0 EndX=18 EndY=7.06359 EndZ=0
    g281: ArcOfCircle CenterX=18.3 CenterY=7.7 CenterZ=0 NormalX=0 NormalY=0 NormalZ=1 AngleXU=0 Radius=0.3 StartAngle=1.5708 EndAngle=3.14159
    g282: LineSegment StartX=18.3 StartY=8 StartZ=0 EndX=21.7 EndY=8 EndZ=0
    g283: ArcOfCircle CenterX=21.7 CenterY=7.7 CenterZ=0 NormalX=0 NormalY=0 NormalZ=1 AngleXU=0 Radius=0.3 StartAngle=0 EndAngle=1.5708
    g284: LineSegment StartX=22 StartY=7.7 StartZ=0 EndX=22 EndY=7.06361 EndZ=0
    g285: ArcOfCircle CenterX=22.3 CenterY=7.06361 CenterZ=0 NormalX=0 NormalY=0 NormalZ=1 AngleXU=0 Radius=0.3 StartAngle=3.14159 EndAngle=3.92699
    g286: Circle CenterX=30 CenterY=0 CenterZ=0 NormalX=0 NormalY=0 NormalZ=-1 AngleXU=0 Radius=2.1
  constraints (403):
    c: Horizontal(g0)
    c: Coincident(g0,g1)
    c: Coincident(g1,g2)
    c: Vertical(g2)
    c: Coincident(g2,g3)
    c: Coincident(g3,g4)
    c: Horizontal(g4)
    c: Coincident(g4,g5)
    c: Vertical(g5)
    c: Coincident(g5,g6)
    c: Coincident(g6,g7)
    c: Horizontal(g7)
    c: Coincident(g7,g8)
    c: Coincident(g8,g9)
    c: Coincident(g9,g10)
    c: Coincident(g10,g11)
    c: Coincident(g11,g12)
    c: Coincident(g12,g13)
    c: Coincident(g13,g14)
    c: Horizontal(g14)
    c: Coincident(g14,g15)
    c: Coincident(g15,g16)
    c: Vertical(g16)
    c: Coincident(g16,g17)
    c: Horizontal(g17)
    c: Coincident(g17,g18)
    c: Coincident(g18,g19)
    c: Vertical(g19)
    c: Coincident(g19,g20)
    c: Coincident(g20,g21)
    c: Horizontal(g21)
    c: Coincident(g21,g22)
    c: Coincident(g22,g23)
    c: Vertical(g23)
    c: Coincident(g23,g24)
    c: Coincident(g24,g25)
    c: Horizontal(g25)
    c: Coincident(g25,g26)
    c: Vertical(g26)
    c: Coincident(g26,g27)
    c: Coincident(g27,g28)
    c: Horizontal(g28)
    c: Coincident(g28,g29)
    c: Coincident(g29,g30)
    c: Coincident(g30,g31)
    c: Coincident(g31,g32)
    c: Coincident(g32,g33)
    c: Coincident(g33,g34)
    c: Coincident(g34,g35)
    c: Horizontal(g35)
    c: Coincident(g35,g36)
    c: Coincident(g36,g37)
    c: Vertical(g37)
    c: Coincident(g37,g38)
    c: Horizontal(g38)
    c: Coincident(g38,g39)
    c: Coincident(g39,g40)
    c: Vertical(g40)
    c: Coincident(g40,g41)
    c: Coincident(g41,g42)
    c: Horizontal(g42)
    c: Coincident(g42,g43)
    c: Horizontal(g43)
    c: Coincident(g43,g44)
    c: Coincident(g44,g45)
    c: Vertical(g45)
    c: Coincident(g45,g46)
    c: Coincident(g46,g47)
    c: Horizontal(g47)
    c: Coincident(g47,g48)
    c: Vertical(g48)
    c: Coincident(g48,g49)
    c: Coincident(g49,g50)
    c: Horizontal(g50)
    c: Coincident(g50,g51)
    c: Coincident(g51,g52)
    c: Coincident(g52,g53)
    c: Coincident(g53,g54)
    c: Coincident(g54,g55)
    c: Coincident(g55,g56)
    c: Coincident(g56,g57)
    c: Horizontal(g57)
    c: Coincident(g57,g58)
    c: Coincident(g58,g59)
    c: Vertical(g59)
    c: Coincident(g59,g60)
    c: Horizontal(g60)
    c: Coincident(g60,g61)
    c: Coincident(g61,g62)
    c: Vertical(g62)
    c: Coincident(g62,g63)
    c: Coincident(g63,g64)
    c: Horizontal(g64)
    c: Coincident(g64,g65)
    c: Coincident(g65,g66)
    c: Vertical(g66)
    c: Coincident(g66,g67)
    c: Coincident(g67,g68)
    c: Horizontal(g68)
    c: Coincident(g68,g69)
    c: Vertical(g69)
    c: Coincident(g69,g70)
    c: Coincident(g70,g71)
    c: Horizontal(g71)
    c: Coincident(g71,g72)
    c: Coincident(g72,g73)
    c: Coincident(g73,g74)
    c: Coincident(g74,g75)
    c: Coincident(g75,g76)
    c: Coincident(g76,g77)
    c: Coincident(g77,g78)
    c: Horizontal(g78)
    c: Coincident(g78,g79)
    c: Coincident(g79,g80)
    c: Vertical(g80)
    c: Coincident(g80,g81)
    c: Horizontal(g81)
    c: Coincident(g81,g82)
    c: Coincident(g82,g83)
    c: Vertical(g83)
    c: Coincident(g83,g84)
    c: Coincident(g84,g85)
    c: Horizontal(g85)
    c: Coincident(g85,g86)
    c: Coincident(g86,g87)
    c: Vertical(g87)
    c: Coincident(g87,g88)
    c: Coincident(g88,g89)
    c: Horizontal(g89)
    c: Coincident(g89,g90)
    c: Coincident(g90,g91)
    c: Vertical(g91)
    c: Coincident(g91,g92)
    c: Horizontal(g92)
    c: Coincident(g92,g93)
    c: Coincident(g93,g94)
    c: Vertical(g94)
    c: Coincident(g94,g95)
    c: Coincident(g95,g96)
    c: Coincident(g96,g97)
    c: Coincident(g97,g98)
    c: Coincident(g98,g99)
    c: Coincident(g99,g100)
    c: Coincident(g100,g101)
    c: Vertical(g101)
    c: Coincident(g101,g102)
    c: Coincident(g102,g103)
    c: Horizontal(g103)
    c: Coincident(g103,g104)
    c: Vertical(g104)
    c: Coincident(g104,g105)
    c: Coincident(g105,g106)
    c: Horizontal(g106)
    c: Coincident(g106,g107)
    c: Coincident(g107,g108)
    c: Vertical(g108)
    c: Coincident(g108,g109)
    c: Coincident(g109,g110)
    c: Horizontal(g110)
    c: Coincident(g110,g111)
    c: Coincident(g111,g112)
    c: Vertical(g112)
    c: Coincident(g112,g113)
    c: Coincident(g113,g114)
    c: Horizontal(g114)
    c: Coincident(g114,g115)
    c: Vertical(g115)
    c: Coincident(g115,g116)
    c: Coincident(g116,g117)
    c: Horizontal(g117)
    c: Coincident(g117,g118)
    c: Coincident(g118,g119)
    c: Coincident(g119,g120)
    c: Coincident(g120,g121)
    c: Coincident(g121,g122)
    c: Coincident(g122,g123)
    c: Coincident(g123,g124)
    c: Horizontal(g124)
    c: Coincident(g124,g125)
    c: Coincident(g125,g126)
    c: Vertical(g126)
    c: Coincident(g126,g127)
    c: Horizontal(g127)
    c: Coincident(g127,g128)
    c: Coincident(g128,g129)
    c: Vertical(g129)
    c: Coincident(g129,g130)
    c: Coincident(g130,g131)
    c: Horizontal(g131)
    c: Coincident(g131,g132)
    c: Coincident(g132,g133)
    c: Vertical(g133)
    c: Coincident(g133,g134)
    c: Coincident(g134,g135)
    c: Horizontal(g135)
    c: Coincident(g135,g136)
    c: Vertical(g136)
    c: Coincident(g136,g137)
    c: Coincident(g137,g138)
    c: Horizontal(g138)
    c: Coincident(g138,g139)
    c: Coincident(g139,g140)
    c: Coincident(g140,g141)
    c: Coincident(g141,g142)
    c: Coincident(g142,g143)
    c: Coincident(g143,g144)
    c: Coincident(g144,g145)
    c: Horizontal(g145)
    c: Coincident(g145,g146)
    c: Coincident(g146,g147)
    c: Vertical(g147)
    c: Coincident(g147,g148)
    c: Horizontal(g148)
    c: Coincident(g148,g149)
    c: Coincident(g149,g150)
    c: Vertical(g150)
    c: Coincident(g150,g151)
    c: Coincident(g151,g152)
    c: Horizontal(g152)
    c: Coincident(g152,g153)
    c: Horizontal(g153)
    c: Coincident(g153,g154)
    c: Coincident(g154,g155)
    c: Vertical(g155)
    c: Coincident(g155,g156)
    c: Coincident(g156,g157)
    c: Horizontal(g157)
    c: Coincident(g157,g158)
    c: Vertical(g158)
    c: Coincident(g158,g159)
    c: Coincident(g159,g160)
    c: Horizontal(g160)
    c: Coincident(g160,g161)
    c: Coincident(g161,g162)
    c: Coincident(g162,g163)
    c: Coincident(g163,g164)
    c: Coincident(g164,g165)
    c: Coincident(g165,g166)
    c: Coincident(g166,g167)
    c: Horizontal(g167)
    c: Coincident(g167,g168)
    c: Coincident(g168,g169)
    c: Vertical(g169)
    c: Coincident(g169,g170)
    c: Horizontal(g170)
    c: Coincident(g170,g171)
    c: Coincident(g171,g172)
    c: Vertical(g172)
    c: Coincident(g172,g173)
    c: Coincident(g173,g174)
    c: Horizontal(g174)
    c: Coincident(g174,g175)
    c: Coincident(g175,g176)
    c: Vertical(g176)
    c: Coincident(g176,g177)
    c: Coincident(g177,g178)
    c: Horizontal(g178)
    c: Coincident(g178,g179)
    c: Vertical(g179)
    c: Coincident(g179,g180)
    c: Coincident(g180,g181)
    c: Horizontal(g181)
    c: Coincident(g181,g182)
    c: Coincident(g182,g183)
    c: Coincident(g183,g184)
    c: Coincident(g184,g185)
    c: Coincident(g185,g186)
    c: Coincident(g186,g187)
    c: Coincident(g187,g188)
    c: Horizontal(g188)
    c: Coincident(g188,g189)
    c: Coincident(g189,g190)
    c: Vertical(g190)
    c: Coincident(g190,g191)
    c: Horizontal(g191)
    c: Coincident(g191,g192)
    c: Coincident(g192,g193)
    c: Vertical(g193)
    c: Coincident(g193,g194)
    c: Coincident(g194,g195)
    c: Horizontal(g195)
    c: Coincident(g195,g196)
    c: Coincident(g196,g197)
    c: Vertical(g197)
    c: Coincident(g197,g198)
    c: Coincident(g198,g199)
    c: Horizontal(g199)
    c: Coincident(g199,g200)
    c: Coincident(g200,g201)
    c: Vertical(g201)
    c: Coincident(g201,g202)
    c: Horizontal(g202)
    c: Coincident(g202,g203)
    c: Coincident(g203,g204)
    c: Vertical(g204)
    c: Coincident(g204,g205)
    c: Coincident(g205,g206)
    c: Coincident(g206,g207)
    c: Coincident(g207,g208)
    c: Coincident(g208,g209)
    c: Coincident(g209,g210)
    c: Coincident(g210,g211)
    c: Vertical(g211)
    c: Coincident(g211,g212)
    c: Coincident(g212,g213)
    c: Horizontal(g213)
    c: Coincident(g213,g214)
    c: Vertical(g214)
    c: Coincident(g214,g215)
    c: Coincident(g215,g216)
    c: Horizontal(g216)
    c: Coincident(g216,g217)
    c: Coincident(g217,g218)
    c: Vertical(g218)
    c: Coincident(g218,g219)
    c: Coincident(g219,g0)
    c: Coincident(g220,g221)
    c: Coincident(g221,g222)
    c: Coincident(g222,g223)
    c: Vertical(g223)
    c: Coincident(g223,g224)
    c: Coincident(g224,g225)
    c: Coincident(g225,g226)
    c: Vertical(g226)
    c: Coincident(g226,g227)
    c: Coincident(g227,g228)
    c: Horizontal(g228)
    c: Coincident(g228,g229)
    c: Coincident(g229,g230)
    c: Vertical(g230)
    c: Coincident(g230,g231)
    c: Coincident(g231,g232)
    c: Coincident(g232,g233)
    c: Coincident(g233,g234)
    c: Coincident(g234,g235)
    c: Coincident(g235,g236)
    c: Vertical(g236)
    c: Coincident(g236,g237)
    c: Coincident(g237,g238)
    c: Horizontal(g238)
    c: Coincident(g238,g239)
    c: Coincident(g239,g240)
    c: Vertical(g240)
    c: Coincident(g240,g220)
    c: Horizontal(g243)
    c: Coincident(g243,g244)
    c: Coincident(g244,g245)
    c: Vertical(g245)
    c: Coincident(g245,g246)
    c: Coincident(g246,g247)
    c: Coincident(g247,g248)
    c: Vertical(g248)
    c: Coincident(g248,g249)
    c: Coincident(g249,g250)
    c: Coincident(g250,g251)
    c: Vertical(g251)
    c: Coincident(g251,g252)
    c: Coincident(g252,g253)
    c: Horizontal(g253)
    c: Coincident(g253,g254)
    c: Horizontal(g254)
    c: Coincident(g254,g255)
    c: Coincident(g255,g256)
    c: Vertical(g256)
    c: Coincident(g256,g257)
    c: Coincident(g257,g258)
    c: Coincident(g258,g259)
    c: Coincident(g259,g260)
    c: Coincident(g260,g261)
    c: Coincident(g261,g262)
    c: Vertical(g262)
    c: Coincident(g262,g263)
    c: Coincident(g263,g264)
    c: Horizontal(g264)
    c: Coincident(g264,g243)
    c: Coincident(g266,g267)
    c: Vertical(g267)
    c: Coincident(g267,g268)
    c: Coincident(g268,g269)
    c: Coincident(g269,g270)
    c: Vertical(g270)
    c: Coincident(g270,g271)
    c: Coincident(g271,g272)
    c: Horizontal(g272)
    c: Coincident(g272,g273)
    c: Coincident(g273,g274)
    c: Vertical(g274)
    c: Coincident(g274,g275)
    c: Coincident(g275,g276)
    c: Coincident(g276,g277)
    c: Vertical(g277)
    c: Coincident(g277,g278)
    c: Coincident(g278,g279)
    c: Coincident(g279,g280)
    c: Vertical(g280)
    c: Coincident(g280,g281)
    c: Coincident(g281,g282)
    c: Horizontal(g282)
    c: Coincident(g282,g283)
    c: Coincident(g283,g284)
    c: Vertical(g284)
    c: Coincident(g284,g285)
    c: Coincident(g285,g266)
FEATURE [Sketcher::SketchObject] Sketch002  label="4040-8"
  ArcFitTolerance = 1e-06
  FullyConstrained = false
  MakeInternals = false
  sketch-geometry (191):
    g0: LineSegment StartX=-17.0607 StartY=4 StartZ=0 EndX=-14 EndY=7.06068 EndZ=0
    g1: LineSegment StartX=-13.2322 StartY=5.7071 StartZ=0 EndX=-17.0607 EndY=1.87865 EndZ=0
    g2: LineSegment StartX=14 StartY=7.06068 StartZ=0 EndX=17.0607 EndY=4 EndZ=0
    g3: LineSegment StartX=17.0607 StartY=1.87866 StartZ=0 EndX=13.2322 EndY=5.70711 EndZ=0
    g4: ArcOfCircle CenterX=12.5251 CenterY=5 CenterZ=0 NormalX=0 NormalY=0 NormalZ=1 AngleXU=0 Radius=1 StartAngle=0.785398 EndAngle=1.5708
    g5: LineSegment StartX=-7.06066 StartY=-14 StartZ=0 EndX=-4 EndY=-17.0607 EndZ=0
    g6: LineSegment StartX=-5.70711 StartY=-13.2322 StartZ=0 EndX=-2.08959 EndY=-16.8498 EndZ=0
    g7: ArcOfCircle CenterX=-5 CenterY=-12.5251 CenterZ=0 NormalX=0 NormalY=0 NormalZ=1 AngleXU=0 Radius=1 StartAngle=3.14159 EndAngle=3.92699
    g8: LineSegment StartX=-17.0607 StartY=-4 StartZ=0 EndX=-14 EndY=-7.06068 EndZ=0
    g9: LineSegment StartX=-13.2323 StartY=-5.70711 StartZ=0 EndX=-17.0607 EndY=-1.87868 EndZ=0
    g10: LineSegment StartX=-14 StartY=-12.9393 StartZ=0 EndX=-17.0607 EndY=-16 EndZ=0
    g11: LineSegment StartX=-16 StartY=-17.0607 StartZ=0 EndX=-12.9394 EndY=-14 EndZ=0
    g12: LineSegment StartX=-17.0607 StartY=-1.87868 StartZ=0 EndX=-18 EndY=-1.87868 EndZ=0
    g13: LineSegment StartX=-17.0607 StartY=1.87865 StartZ=0 EndX=-18 EndY=1.87865 EndZ=0
    g14: LineSegment StartX=1.99997 StartY=-17.6973 StartZ=0 EndX=1.99997 EndY=-17.0663 EndZ=0
    g15: LineSegment StartX=-2.00001 StartY=-17.0663 StartZ=0 EndX=-2.00001 EndY=-17.6973 EndZ=0
    g16: LineSegment StartX=-1.70003 StartY=-18 StartZ=0 EndX=1.69999 EndY=-18 EndZ=0
    g17: ArcOfCircle CenterX=-1.70003 CenterY=-17.7 CenterZ=0 NormalX=0 NormalY=0 NormalZ=1 AngleXU=0 Radius=0.3 StartAngle=3.13263 EndAngle=4.71239
    g18: ArcOfCircle CenterX=1.69999 CenterY=-17.7 CenterZ=0 NormalX=0 NormalY=0 NormalZ=1 AngleXU=0 Radius=0.3 StartAngle=4.71239 EndAngle=6.29215
    g19: LineSegment StartX=4 StartY=-17.0607 StartZ=0 EndX=7.06066 EndY=-14 EndZ=0
    g20: LineSegment StartX=2.08955 StartY=-16.8498 StartZ=0 EndX=5.70711 EndY=-13.2322 EndZ=0
    g21: ArcOfCircle CenterX=-2.3 CenterY=-17.0636 CenterZ=0 NormalX=0 NormalY=0 NormalZ=1 AngleXU=0 Radius=0.3 StartAngle=6.27414 EndAngle=7.07667
    g22: ArcOfCircle CenterX=2.29996 CenterY=-17.0636 CenterZ=0 NormalX=0 NormalY=0 NormalZ=1 AngleXU=0 Radius=0.3 StartAngle=2.3481 EndAngle=3.15063
    g23: LineSegment StartX=17.0607 StartY=-1.87868 StartZ=0 EndX=13.2323 EndY=-5.70711 EndZ=0
    g24: ArcOfCircle CenterX=12.5252 CenterY=-5 CenterZ=0 NormalX=0 NormalY=0 NormalZ=1 AngleXU=0 Radius=1 StartAngle=4.71239 EndAngle=5.49779
    g25: LineSegment StartX=14 StartY=-7.06068 StartZ=0 EndX=17.0607 EndY=-4 EndZ=0
    g26: LineSegment StartX=12.9394 StartY=-14 StartZ=0 EndX=16 EndY=-17.0607 EndZ=0
    g27: LineSegment StartX=17.0607 StartY=-1.87868 StartZ=0 EndX=18 EndY=-1.87868 EndZ=0
    g28: LineSegment StartX=17.0607 StartY=1.87866 StartZ=0 EndX=18 EndY=1.87866 EndZ=0
    g29: LineSegment StartX=-5.70711 StartY=13.2322 StartZ=0 EndX=-2.0896 EndY=16.8498 EndZ=0
    g30: ArcOfCircle CenterX=-5 CenterY=12.5251 CenterZ=0 NormalX=0 NormalY=0 NormalZ=1 AngleXU=0 Radius=1 StartAngle=2.3562 EndAngle=3.14159
    g31: LineSegment StartX=-7.06064 StartY=14 StartZ=0 EndX=-4 EndY=17.0606 EndZ=0
    g32: LineSegment StartX=-14 StartY=12.9393 StartZ=0 EndX=-17.0607 EndY=16 EndZ=0
    g33: LineSegment StartX=-16 StartY=17.0606 StartZ=0 EndX=-12.9394 EndY=14 EndZ=0
    g34: LineSegment StartX=1.99996 StartY=17.6973 StartZ=0 EndX=1.99996 EndY=17.0663 EndZ=0
    g35: LineSegment StartX=-2.00002 StartY=17.0663 StartZ=0 EndX=-2.00002 EndY=17.6973 EndZ=0
    g36: LineSegment StartX=4 StartY=17.0606 StartZ=0 EndX=7.06064 EndY=14 EndZ=0
    g37: LineSegment StartX=2.08954 StartY=16.8498 StartZ=0 EndX=5.70711 EndY=13.2322 EndZ=0
    g38: ArcOfCircle CenterX=-2.30001 CenterY=17.0636 CenterZ=0 NormalX=0 NormalY=0 NormalZ=1 AngleXU=0 Radius=0.3 StartAngle=5.4897 EndAngle=6.29223
    g39: ArcOfCircle CenterX=2.29995 CenterY=17.0636 CenterZ=0 NormalX=0 NormalY=0 NormalZ=1 AngleXU=0 Radius=0.3 StartAngle=3.13255 EndAngle=3.93508
    g40: LineSegment StartX=-1.70004 StartY=18 StartZ=0 EndX=1.69997 EndY=18 EndZ=0
    g41: ArcOfCircle CenterX=-1.70004 CenterY=17.7 CenterZ=0 NormalX=0 NormalY=0 NormalZ=1 AngleXU=0 Radius=0.3 StartAngle=1.5708 EndAngle=3.15056
    g42: ArcOfCircle CenterX=1.69997 CenterY=17.7 CenterZ=0 NormalX=0 NormalY=0 NormalZ=1 AngleXU=0 Radius=0.3 StartAngle=6.27422 EndAngle=7.85398
    g43: LineSegment StartX=17.0607 StartY=16 StartZ=0 EndX=14 EndY=12.9393 EndZ=0
    g44: LineSegment StartX=12.9394 StartY=14 StartZ=0 EndX=16 EndY=17.0606 EndZ=0
    g45: LineSegment StartX=-20 StartY=19 StartZ=0 EndX=-20 EndY=13.3 EndZ=0
    g46: LineSegment StartX=20 StartY=19 StartZ=0 EndX=20 EndY=13.3 EndZ=0
    g47: LineSegment StartX=-19 StartY=20 StartZ=0 EndX=-13.3 EndY=20 EndZ=0
    g48: LineSegment StartX=-19 StartY=-20 StartZ=0 EndX=-13.3 EndY=-20 EndZ=0
    g49: ArcOfCircle CenterX=-19 CenterY=-19 CenterZ=0 NormalX=0 NormalY=0 NormalZ=1 AngleXU=0 Radius=1 StartAngle=3.14159 EndAngle=4.71239
    g50: ArcOfCircle CenterX=19 CenterY=-19 CenterZ=0 NormalX=0 NormalY=0 NormalZ=1 AngleXU=0 Radius=1 StartAngle=4.71239 EndAngle=6.28319
    g51: ArcOfCircle CenterX=19 CenterY=19 CenterZ=0 NormalX=0 NormalY=0 NormalZ=1 AngleXU=0 Radius=1 StartAngle=0 EndAngle=1.5708
    g52: ArcOfCircle CenterX=-19 CenterY=19 CenterZ=0 NormalX=0 NormalY=0 NormalZ=1 AngleXU=0 Radius=1 StartAngle=1.5708 EndAngle=3.14159
    g53: LineSegment StartX=-16 StartY=18 StartZ=0 EndX=-13.3 EndY=18 EndZ=0
    g54: LineSegment StartX=-16 StartY=-18 StartZ=0 EndX=-13.3 EndY=-18 EndZ=0
    g55: LineSegment StartX=-6.7 StartY=18 StartZ=0 EndX=-4 EndY=18 EndZ=0
    g56: ArcOfCircle CenterX=-6.7 CenterY=18.3 CenterZ=0 NormalX=0 NormalY=0 NormalZ=1 AngleXU=0 Radius=0.3 StartAngle=3.14159 EndAngle=4.71239
    g57: LineSegment StartX=13.3 StartY=18 StartZ=0 EndX=16 EndY=18 EndZ=0
    g58: LineSegment StartX=-16 StartY=18 StartZ=0 EndX=-16 EndY=17.0606 EndZ=0
    g59: LineSegment StartX=-4 StartY=18 StartZ=0 EndX=-4 EndY=17.0606 EndZ=0
    g60: LineSegment StartX=-13 StartY=19.7 StartZ=0 EndX=-13 EndY=18.3 EndZ=0
    g61: ArcOfCircle CenterX=-13.3 CenterY=18.3 CenterZ=0 NormalX=0 NormalY=0 NormalZ=1 AngleXU=0 Radius=0.3 StartAngle=4.71239 EndAngle=6.28319
    g62: LineSegment StartX=-7 StartY=19.7 StartZ=0 EndX=-7 EndY=18.3 EndZ=0
    g63: LineSegment StartX=-6.7 StartY=20 StartZ=0 EndX=6.7 EndY=20 EndZ=0
    g64: LineSegment StartX=7 StartY=19.7 StartZ=0 EndX=7 EndY=18.3 EndZ=0
    g65: ArcOfCircle CenterX=6.7 CenterY=18.3 CenterZ=0 NormalX=0 NormalY=0 NormalZ=1 AngleXU=0 Radius=0.3 StartAngle=4.71239 EndAngle=6.28319
    g66: LineSegment StartX=13 StartY=19.7 StartZ=0 EndX=13 EndY=18.3 EndZ=0
    g67: ArcOfCircle CenterX=13.3 CenterY=18.3 CenterZ=0 NormalX=0 NormalY=0 NormalZ=1 AngleXU=0 Radius=0.3 StartAngle=3.14159 EndAngle=4.71239
    g68: LineSegment StartX=13.3 StartY=20 StartZ=0 EndX=19 EndY=20 EndZ=0
    g69: LineSegment StartX=4 StartY=18 StartZ=0 EndX=6.7 EndY=18 EndZ=0
    g70: LineSegment StartX=4 StartY=18 StartZ=0 EndX=4 EndY=17.0606 EndZ=0
    g71: LineSegment StartX=16 StartY=18 StartZ=0 EndX=16 EndY=17.0606 EndZ=0
    g72: LineSegment StartX=-6 StartY=12.5251 StartZ=0 EndX=-6 EndY=10.1693 EndZ=0
    g73: LineSegment StartX=-18 StartY=16 StartZ=0 EndX=-18 EndY=13.3 EndZ=0
    g74: LineSegment StartX=4 StartY=-17.0607 StartZ=0 EndX=4 EndY=-18 EndZ=0
    g75: LineSegment StartX=16 StartY=-17.0607 StartZ=0 EndX=16 EndY=-18 EndZ=0
    g76: LineSegment StartX=13.3 StartY=-20 StartZ=0 EndX=19 EndY=-20 EndZ=0
    g77: LineSegment StartX=7 StartY=-18.3 StartZ=0 EndX=7 EndY=-19.7 EndZ=0
    g78: ArcOfCircle CenterX=6.7 CenterY=-18.3 CenterZ=0 NormalX=0 NormalY=0 NormalZ=1 AngleXU=0 Radius=0.3 StartAngle=0 EndAngle=1.5708
    g79: LineSegment StartX=13.3 StartY=-18 StartZ=0 EndX=16 EndY=-18 EndZ=0
    g80: ArcOfCircle CenterX=13.3 CenterY=-18.3 CenterZ=0 NormalX=0 NormalY=0 NormalZ=1 AngleXU=0 Radius=0.3 StartAngle=1.5708 EndAngle=3.14159
    g81: LineSegment StartX=-13 StartY=-18.3 StartZ=0 EndX=-13 EndY=-19.7 EndZ=0
    g82: ArcOfCircle CenterX=-13.3 CenterY=-18.3 CenterZ=0 NormalX=0 NormalY=0 NormalZ=1 AngleXU=0 Radius=0.3 StartAngle=0 EndAngle=1.5708
    g83: LineSegment StartX=-7 StartY=-18.3 StartZ=0 EndX=-7 EndY=-19.7 EndZ=0
    g84: LineSegment StartX=-16 StartY=-17.0607 StartZ=0 EndX=-16 EndY=-18 EndZ=0
    g85: LineSegment StartX=-4 StartY=-17.0607 StartZ=0 EndX=-4 EndY=-18 EndZ=0
    g86: LineSegment StartX=4 StartY=-18 StartZ=0 EndX=6.7 EndY=-18 EndZ=0
    g87: LineSegment StartX=-6.7 StartY=-18 StartZ=0 EndX=-4 EndY=-18 EndZ=0
    g88: ArcOfCircle CenterX=-6.7 CenterY=-18.3 CenterZ=0 NormalX=0 NormalY=0 NormalZ=1 AngleXU=0 Radius=0.3 StartAngle=1.5708 EndAngle=3.14159
    g89: LineSegment StartX=-6.7 StartY=-20 StartZ=0 EndX=6.7 EndY=-20 EndZ=0
    g90: LineSegment StartX=18 StartY=16 StartZ=0 EndX=18 EndY=13.3 EndZ=0
    g91: LineSegment StartX=18.3 StartY=-7 StartZ=0 EndX=19.7 EndY=-7 EndZ=0
    g92: ArcOfCircle CenterX=18.3 CenterY=-6.7 CenterZ=0 NormalX=0 NormalY=0 NormalZ=1 AngleXU=0 Radius=0.3 StartAngle=3.14159 EndAngle=4.71239
    g93: LineSegment StartX=18.3 StartY=-13 StartZ=0 EndX=19.7 EndY=-13 EndZ=0
    g94: ArcOfCircle CenterX=18.3 CenterY=-13.3 CenterZ=0 NormalX=0 NormalY=0 NormalZ=1 AngleXU=0 Radius=0.3 StartAngle=1.5708 EndAngle=3.14159
    g95: LineSegment StartX=20 StartY=-13.3 StartZ=0 EndX=20 EndY=-19 EndZ=0
    g96: LineSegment StartX=18 StartY=-13.3 StartZ=0 EndX=18 EndY=-16 EndZ=0
    g97: LineSegment StartX=18.3 StartY=13 StartZ=0 EndX=19.7 EndY=13 EndZ=0
    g98: ArcOfCircle CenterX=18.3 CenterY=13.3 CenterZ=0 NormalX=0 NormalY=0 NormalZ=1 AngleXU=0 Radius=0.3 StartAngle=3.14159 EndAngle=4.71239
    g99: LineSegment StartX=18.3 StartY=7 StartZ=0 EndX=19.7 EndY=7 EndZ=0
    g100: ArcOfCircle CenterX=18.3 CenterY=6.7 CenterZ=0 NormalX=0 NormalY=0 NormalZ=1 AngleXU=0 Radius=0.3 StartAngle=1.5708 EndAngle=3.14159
    g101: LineSegment StartX=18 StartY=6.7 StartZ=0 EndX=18 EndY=4 EndZ=0
    g102: LineSegment StartX=20 StartY=6.7 StartZ=0 EndX=20 EndY=-6.7 EndZ=0
    g103: LineSegment StartX=17.0607 StartY=4 StartZ=0 EndX=18 EndY=4 EndZ=0
    g104: LineSegment StartX=17.0607 StartY=16 StartZ=0 EndX=18 EndY=16 EndZ=0
    g105: LineSegment StartX=17.0607 StartY=-4 StartZ=0 EndX=18 EndY=-4 EndZ=0
    g106: LineSegment StartX=17.0607 StartY=-16 StartZ=0 EndX=18 EndY=-16 EndZ=0
    g107: LineSegment StartX=18 StartY=-4 StartZ=0 EndX=18 EndY=-6.7 EndZ=0
    g108: LineSegment StartX=-19.7 StartY=13 StartZ=0 EndX=-18.3 EndY=13 EndZ=0
    g109: ArcOfCircle CenterX=-18.3 CenterY=13.3 CenterZ=0 NormalX=0 NormalY=0 NormalZ=1 AngleXU=0 Radius=0.3 StartAngle=4.71239 EndAngle=6.28319
    g110: LineSegment StartX=-19.7 StartY=7 StartZ=0 EndX=-18.3 EndY=7 EndZ=0
    g111: ArcOfCircle CenterX=-18.3 CenterY=6.7 CenterZ=0 NormalX=0 NormalY=0 NormalZ=1 AngleXU=0 Radius=0.3 StartAngle=0 EndAngle=1.5708
    g112: LineSegment StartX=-19.7 StartY=-7 StartZ=0 EndX=-18.3 EndY=-7 EndZ=0
    g113: LineSegment StartX=-19.7 StartY=-13 StartZ=0 EndX=-18.3 EndY=-13 EndZ=0
    g114: LineSegment StartX=-18 StartY=-4 StartZ=0 EndX=-18 EndY=-6.7 EndZ=0
    g115: ArcOfCircle CenterX=-18.3 CenterY=-6.7 CenterZ=0 NormalX=0 NormalY=0 NormalZ=1 AngleXU=0 Radius=0.3 StartAngle=4.71239 EndAngle=6.28319
    g116: LineSegment StartX=-20 StartY=6.7 StartZ=0 EndX=-20 EndY=-6.7 EndZ=0
    g117: LineSegment StartX=-18 StartY=-13.3 StartZ=0 EndX=-18 EndY=-16 EndZ=0
    g118: ArcOfCircle CenterX=-18.3 CenterY=-13.3 CenterZ=0 NormalX=0 NormalY=0 NormalZ=1 AngleXU=0 Radius=0.3 StartAngle=0 EndAngle=1.5708
    g119: LineSegment StartX=-20 StartY=-13.3 StartZ=0 EndX=-20 EndY=-19 EndZ=0
    g120: LineSegment StartX=-18 StartY=16 StartZ=0 EndX=-17.0607 EndY=16 EndZ=0
    g121: LineSegment StartX=-18 StartY=4 StartZ=0 EndX=-17.0607 EndY=4 EndZ=0
    g122: LineSegment StartX=-18 StartY=-4 StartZ=0 EndX=-17.0607 EndY=-4 EndZ=0
    g123: LineSegment StartX=-18 StartY=-16 StartZ=0 EndX=-17.0607 EndY=-16 EndZ=0
    g124: LineSegment StartX=-18 StartY=6.7 StartZ=0 EndX=-18 EndY=4 EndZ=0
    g125: LineSegment StartX=-18 StartY=1.87865 StartZ=0 EndX=-18 EndY=-1.87868 EndZ=0
    g126: LineSegment StartX=-12.5251 StartY=6 StartZ=0 EndX=-10.1693 EndY=6 EndZ=0
    g127: ArcOfCircle CenterX=-12.5251 CenterY=5 CenterZ=0 NormalX=0 NormalY=0 NormalZ=1 AngleXU=0 Radius=1 StartAngle=1.5708 EndAngle=2.3562
    g128: LineSegment StartX=13 StartY=-18.3 StartZ=0 EndX=13 EndY=-19.7 EndZ=0
    g129: ArcOfCircle CenterX=-13.3 CenterY=19.7 CenterZ=0 NormalX=0 NormalY=0 NormalZ=1 AngleXU=0 Radius=0.3 StartAngle=0 EndAngle=1.5708
    g130: ArcOfCircle CenterX=-6.7 CenterY=19.7 CenterZ=0 NormalX=0 NormalY=0 NormalZ=1 AngleXU=0 Radius=0.3 StartAngle=1.5708 EndAngle=3.14159
    g131: ArcOfCircle CenterX=6.7 CenterY=19.7 CenterZ=0 NormalX=0 NormalY=0 NormalZ=1 AngleXU=0 Radius=0.3 StartAngle=0 EndAngle=1.5708
    g132: ArcOfCircle CenterX=13.3 CenterY=19.7 CenterZ=0 NormalX=0 NormalY=0 NormalZ=1 AngleXU=0 Radius=0.3 StartAngle=1.5708 EndAngle=3.14159
    g133: ArcOfCircle CenterX=19.7 CenterY=13.3 CenterZ=0 NormalX=0 NormalY=0 NormalZ=1 AngleXU=0 Radius=0.3 StartAngle=4.71239 EndAngle=6.28319
    g134: ArcOfCircle CenterX=19.7 CenterY=6.7 CenterZ=0 NormalX=0 NormalY=0 NormalZ=1 AngleXU=0 Radius=0.3 StartAngle=0 EndAngle=1.5708
    g135: ArcOfCircle CenterX=19.7 CenterY=-6.7 CenterZ=0 NormalX=0 NormalY=0 NormalZ=1 AngleXU=0 Radius=0.3 StartAngle=4.71239 EndAngle=6.28319
    g136: ArcOfCircle CenterX=19.7 CenterY=-13.3 CenterZ=0 NormalX=0 NormalY=0 NormalZ=1 AngleXU=0 Radius=0.3 StartAngle=0 EndAngle=1.5708
    g137: ArcOfCircle CenterX=13.3 CenterY=-19.7 CenterZ=0 NormalX=0 NormalY=0 NormalZ=1 AngleXU=0 Radius=0.3 StartAngle=3.14159 EndAngle=4.71239
    g138: ArcOfCircle CenterX=6.7 CenterY=-19.7 CenterZ=0 NormalX=0 NormalY=0 NormalZ=1 AngleXU=0 Radius=0.3 StartAngle=4.71239 EndAngle=6.28319
    g139: ArcOfCircle CenterX=-6.7 CenterY=-19.7 CenterZ=0 NormalX=0 NormalY=0 NormalZ=1 AngleXU=0 Radius=0.3 StartAngle=3.14159 EndAngle=4.71239
    g140: ArcOfCircle CenterX=-13.3 CenterY=-19.7 CenterZ=0 NormalX=0 NormalY=0 NormalZ=1 AngleXU=0 Radius=0.3 StartAngle=4.71239 EndAngle=6.28319
    g141: ArcOfCircle CenterX=-19.7 CenterY=-13.3 CenterZ=0 NormalX=0 NormalY=0 NormalZ=1 AngleXU=0 Radius=0.3 StartAngle=1.5708 EndAngle=3.14159
    g142: ArcOfCircle CenterX=-19.7 CenterY=-6.7 CenterZ=0 NormalX=0 NormalY=0 NormalZ=1 AngleXU=0 Radius=0.3 StartAngle=3.14159 EndAngle=4.71239
    g143: ArcOfCircle CenterX=-19.7 CenterY=6.7 CenterZ=0 NormalX=0 NormalY=0 NormalZ=1 AngleXU=0 Radius=0.3 StartAngle=1.5708 EndAngle=3.14159
    g144: ArcOfCircle CenterX=-19.7 CenterY=13.3 CenterZ=0 NormalX=0 NormalY=0 NormalZ=1 AngleXU=0 Radius=0.3 StartAngle=3.14159 EndAngle=4.71239
    g145: ArcOfCircle CenterX=-10 CenterY=10 CenterZ=0 NormalX=0 NormalY=0 NormalZ=1 AngleXU=0 Radius=2.1 StartAngle=0.0555038 EndAngle=4.65689
    g146: ArcOfCircle CenterX=-6.95235 CenterY=10.1693 CenterZ=0 NormalX=0 NormalY=0 NormalZ=1 AngleXU=0 Radius=0.95235 StartAngle=3.1971 EndAngle=6.28319
    g147: ArcOfCircle CenterX=-10.1693 CenterY=6.95235 CenterZ=0 NormalX=0 NormalY=0 NormalZ=1 AngleXU=0 Radius=0.95235 StartAngle=4.71239 EndAngle=7.79848
    g148: LineSegment StartX=-12.5251 StartY=-6 StartZ=0 EndX=-10.1693 EndY=-6 EndZ=0
    g149: ArcOfCircle CenterX=-12.5251 CenterY=-5 CenterZ=0 NormalX=0 NormalY=0 NormalZ=1 AngleXU=0 Radius=1 StartAngle=3.92699 EndAngle=4.71239
    g150: LineSegment StartX=-6 StartY=-12.5251 StartZ=0 EndX=-6 EndY=-10.1693 EndZ=0
    g151: ArcOfCircle CenterX=-10 CenterY=-10 CenterZ=0 NormalX=0 NormalY=0 NormalZ=1 AngleXU=0 Radius=2.1 StartAngle=1.6263 EndAngle=6.22768
    g152: ArcOfCircle CenterX=-10.1693 CenterY=-6.95235 CenterZ=0 NormalX=0 NormalY=0 NormalZ=1 AngleXU=0 Radius=0.95235 StartAngle=4.76789 EndAngle=7.85398
    g153: ArcOfCircle CenterX=-6.95235 CenterY=-10.1693 CenterZ=0 NormalX=0 NormalY=0 NormalZ=1 AngleXU=0 Radius=0.95235 StartAngle=0 EndAngle=3.08609
    g154: LineSegment StartX=6 StartY=-12.5251 StartZ=0 EndX=6 EndY=-10.1693 EndZ=0
    g155: ArcOfCircle CenterX=5 CenterY=-12.5251 CenterZ=0 NormalX=0 NormalY=0 NormalZ=1 AngleXU=0 Radius=1 StartAngle=5.49779 EndAngle=6.28319
    g156: LineSegment StartX=12.5252 StartY=-6 StartZ=0 EndX=10.1693 EndY=-6 EndZ=0
    g157: ArcOfCircle CenterX=10 CenterY=-10 CenterZ=0 NormalX=0 NormalY=0 NormalZ=1 AngleXU=0 Radius=2.1 StartAngle=3.1971 EndAngle=7.79848
    g158: ArcOfCircle CenterX=6.95235 CenterY=-10.1693 CenterZ=0 NormalX=0 NormalY=0 NormalZ=1 AngleXU=0 Radius=0.95235 StartAngle=0.0555038 EndAngle=3.14159
    g159: ArcOfCircle CenterX=10.1693 CenterY=-6.95235 CenterZ=0 NormalX=0 NormalY=0 NormalZ=1 AngleXU=0 Radius=0.95235 StartAngle=1.5708 EndAngle=4.65689
    g160: LineSegment StartX=12.5251 StartY=6 StartZ=0 EndX=10.1693 EndY=6 EndZ=0
    g161: LineSegment StartX=6 StartY=12.5251 StartZ=0 EndX=6 EndY=10.1693 EndZ=0
    g162: ArcOfCircle CenterX=5 CenterY=12.5251 CenterZ=0 NormalX=0 NormalY=0 NormalZ=1 AngleXU=0 Radius=1 StartAngle=0 EndAngle=0.7854
    g163: ArcOfCircle CenterX=10 CenterY=10 CenterZ=0 NormalX=0 NormalY=0 NormalZ=1 AngleXU=0 Radius=2.1 StartAngle=4.76789 EndAngle=9.36927
    g164: ArcOfCircle CenterX=10.1693 CenterY=6.95235 CenterZ=0 NormalX=0 NormalY=0 NormalZ=1 AngleXU=0 Radius=0.95235 StartAngle=1.6263 EndAngle=4.71239
    g165: ArcOfCircle CenterX=6.95235 CenterY=10.1693 CenterZ=0 NormalX=0 NormalY=0 NormalZ=1 AngleXU=0 Radius=0.95235 StartAngle=3.14159 EndAngle=6.22768
    g166: LineSegment StartX=-7.06064 StartY=14 StartZ=0 EndX=-9.34642 EndY=14 EndZ=0
    g167: LineSegment StartX=-14 StartY=7.06068 StartZ=0 EndX=-14 EndY=7.5 EndZ=0
    g168: LineSegment StartX=-14 StartY=12.9393 StartZ=0 EndX=-14 EndY=10.6536 EndZ=0
    g169: LineSegment StartX=14 StartY=12.9393 StartZ=0 EndX=14 EndY=12.5 EndZ=0
    g170: LineSegment StartX=14 StartY=7.06068 StartZ=0 EndX=14 EndY=9.34641 EndZ=0
    g171: LineSegment StartX=12.9394 StartY=-14 StartZ=0 EndX=12.5 EndY=-14 EndZ=0
    g172: LineSegment StartX=7.06066 StartY=-14 StartZ=0 EndX=9.34642 EndY=-14 EndZ=0
    g173: LineSegment StartX=14 StartY=-7.06068 StartZ=0 EndX=14 EndY=-7.5 EndZ=0
    g174: LineSegment StartX=14 StartY=-12.9393 StartZ=0 EndX=14 EndY=-10.6536 EndZ=0
    g175: LineSegment StartX=7.06064 StartY=14 StartZ=0 EndX=7.5 EndY=14 EndZ=0
    g176: LineSegment StartX=12.9394 StartY=14 StartZ=0 EndX=10.6536 EndY=14 EndZ=0
    g177: LineSegment StartX=-7.06066 StartY=-14 StartZ=0 EndX=-7.5 EndY=-14 EndZ=0
    g178: LineSegment StartX=-12.9394 StartY=-14 StartZ=0 EndX=-10.6536 EndY=-14 EndZ=0
    g179: LineSegment StartX=-14 StartY=-12.9393 StartZ=0 EndX=-14 EndY=-12.5 EndZ=0
    g180: LineSegment StartX=-14 StartY=-7.06068 StartZ=0 EndX=-14 EndY=-9.34641 EndZ=0
    g181: LineSegment StartX=-12.9394 StartY=14 StartZ=0 EndX=-9.34642 EndY=14 EndZ=0
    g182: LineSegment StartX=-14 StartY=10.6536 StartZ=0 EndX=-14 EndY=7.5 EndZ=0
    g183: LineSegment StartX=-14 StartY=-9.34641 StartZ=0 EndX=-14 EndY=-12.5 EndZ=0
    g184: LineSegment StartX=-10.6536 StartY=-14 StartZ=0 EndX=-7.5 EndY=-14 EndZ=0
    g185: LineSegment StartX=9.34642 StartY=-14 StartZ=0 EndX=12.5 EndY=-14 EndZ=0
    g186: LineSegment StartX=14 StartY=-10.6536 StartZ=0 EndX=14 EndY=-7.5 EndZ=0
    g187: LineSegment StartX=14 StartY=12.5 StartZ=0 EndX=14 EndY=9.34641 EndZ=0
    g188: LineSegment StartX=7.5 StartY=14 StartZ=0 EndX=10.6536 EndY=14 EndZ=0
    g189: LineSegment StartX=18 StartY=1.87866 StartZ=0 EndX=18 EndY=-1.87868 EndZ=0
    g190: LineSegment StartX=14 StartY=-12.9393 StartZ=0 EndX=17.0607 EndY=-16 EndZ=0
  constraints (200):
    c: Coincident(g181,g33)
    c: Coincident(g181,g166)
    c: Horizontal(g181)
    c: Coincident(g182,g168)
    c: Coincident(g182,g167)
    c: Vertical(g182)
    c: Coincident(g183,g180)
    c: Coincident(g183,g179)
    c: Vertical(g183)
    c: Coincident(g184,g178)
    c: Coincident(g184,g177)
    c: Horizontal(g184)
    c: Coincident(g185,g172)
    c: Coincident(g185,g171)
    c: Horizontal(g185)
    c: Coincident(g186,g174)
    c: Coincident(g186,g173)
    c: Vertical(g186)
    c: Coincident(g187,g169)
    c: Coincident(g187,g170)
    c: Vertical(g187)
    c: Coincident(g188,g175)
    c: Coincident(g188,g176)
    c: Horizontal(g188)
    c: Coincident(g189,g28)
    c: Coincident(g189,g27)
    c: Vertical(g189)
    c: Coincident(g190,g174)
    c: Coincident(g190,g106)
    c: Coincident(g49,g119)
    c: Coincident(g119,g141)
    c: Coincident(g116,g142)
    c: Coincident(g116,g143)
    c: Coincident(g45,g144)
    c: Coincident(g45,g52)
    c: Coincident(g113,g141)
    c: Coincident(g112,g142)
    c: Coincident(g110,g143)
    c: Coincident(g108,g144)
    c: Coincident(g48,g49)
    c: Coincident(g47,g52)
    c: Coincident(g113,g118)
    c: Coincident(g112,g115)
    c: Coincident(g110,g111)
    c: Coincident(g108,g109)
    c: Coincident(g117,g123)
    c: Coincident(g117,g118)
    c: Coincident(g114,g115)
    c: Coincident(g114,g122)
    c: Coincident(g12,g125)
    c: Coincident(g13,g125)
    c: Coincident(g121,g124)
    c: Coincident(g111,g124)
    c: Coincident(g73,g109)
    c: Coincident(g73,g120)
    c: Coincident(g10,g123)
    c: Coincident(g8,g122)
    c: Coincident(g9,g12)
    c: Coincident(g1,g13)
    c: Coincident(g0,g121)
    c: Coincident(g32,g120)
    c: Coincident(g54,g84)
    c: Coincident(g11,g84)
    c: Coincident(g33,g58)
    c: Coincident(g53,g58)
    c: Coincident(g10,g179)
    c: Coincident(g8,g180)
    c: Coincident(g0,g167)
    c: Coincident(g32,g168)
    c: Coincident(g48,g140)
    c: Coincident(g54,g82)
    c: Coincident(g53,g61)
    c: Coincident(g47,g129)
    c: Coincident(g9,g149)
    c: Coincident(g1,g127)
    c: Coincident(g81,g140)
    c: Coincident(g81,g82)
    c: Coincident(g60,g61)
    c: Coincident(g60,g129)
    c: Coincident(g11,g178)
    c: Coincident(g148,g149)
    c: Coincident(g126,g127)
    c: Coincident(g148,g152)
    c: Coincident(g126,g147)
    c: Coincident(g151,g152)
    c: Coincident(g145,g147)
    c: Coincident(g151,g153)
    c: Coincident(g145,g146)
    c: Coincident(g5,g177)
    c: Coincident(g31,g166)
    c: Coincident(g83,g139)
    c: Coincident(g83,g88)
    c: Coincident(g56,g62)
    c: Coincident(g62,g130)
    c: Coincident(g89,g139)
    c: Coincident(g87,g88)
    c: Coincident(g55,g56)
    c: Coincident(g63,g130)
    c: Coincident(g7,g150)
    c: Coincident(g150,g153)
    c: Coincident(g72,g146)
    c: Coincident(g30,g72)
    c: Coincident(g6,g7)
    c: Coincident(g29,g30)
    c: Coincident(g85,g87)
    c: Coincident(g5,g85)
    c: Coincident(g31,g59)
    c: Coincident(g55,g59)
    c: Coincident(g6,g21)
    c: Coincident(g29,g38)
    c: Coincident(g15,g17)
    c: Coincident(g15,g21)
    c: Coincident(g35,g38)
    c: Coincident(g35,g41)
    c: Coincident(g16,g17)
    c: Coincident(g40,g41)
    c: Coincident(g16,g18)
    c: Coincident(g40,g42)
    c: Coincident(g14,g18)
    c: Coincident(g14,g22)
    c: Coincident(g34,g39)
    c: Coincident(g34,g42)
    c: Coincident(g20,g22)
    c: Coincident(g37,g39)
    c: Coincident(g74,g86)
    c: Coincident(g19,g74)
    c: Coincident(g36,g70)
    c: Coincident(g69,g70)
    c: Coincident(g20,g155)
    c: Coincident(g37,g162)
    c: Coincident(g154,g155)
    c: Coincident(g154,g158)
    c: Coincident(g161,g165)
    c: Coincident(g161,g162)
    c: Coincident(g89,g138)
    c: Coincident(g78,g86)
    c: Coincident(g65,g69)
    c: Coincident(g63,g131)
    c: Coincident(g77,g138)
    c: Coincident(g77,g78)
    c: Coincident(g64,g65)
    c: Coincident(g64,g131)
    c: Coincident(g19,g172)
    c: Coincident(g36,g175)
    c: Coincident(g157,g158)
    c: Coincident(g163,g165)
    c: Coincident(g157,g159)
    c: Coincident(g163,g164)
    c: Coincident(g156,g159)
    c: Coincident(g160,g164)
    c: Coincident(g24,g156)
    c: Coincident(g4,g160)
    c: Coincident(g26,g171)
    c: Coincident(g44,g176)
    c: Coincident(g128,g137)
    c: Coincident(g80,g128)
    c: Coincident(g66,g67)
    c: Coincident(g66,g132)
    c: Coincident(g23,g24)
    c: Coincident(g3,g4)
    c: Coincident(g76,g137)
    c: Coincident(g79,g80)
    c: Coincident(g57,g67)
    c: Coincident(g68,g132)
    c: Coincident(g25,g173)
    c: Coincident(g2,g170)
    c: Coincident(g43,g169)
    c: Coincident(g75,g79)
    c: Coincident(g26,g75)
    c: Coincident(g44,g71)
    c: Coincident(g57,g71)
    c: Coincident(g25,g105)
    c: Coincident(g23,g27)
    c: Coincident(g3,g28)
    c: Coincident(g2,g103)
    c: Coincident(g43,g104)
    c: Coincident(g96,g106)
    c: Coincident(g94,g96)
    c: Coincident(g92,g107)
    c: Coincident(g105,g107)
    c: Coincident(g101,g103)
    c: Coincident(g100,g101)
    c: Coincident(g90,g98)
    c: Coincident(g90,g104)
    c: Coincident(g93,g94)
    c: Coincident(g91,g92)
    c: Coincident(g99,g100)
    c: Coincident(g97,g98)
    c: Coincident(g50,g76)
    c: Coincident(g51,g68)
    c: Coincident(g93,g136)
    c: Coincident(g91,g135)
    c: Coincident(g99,g134)
    c: Coincident(g97,g133)
    c: Coincident(g50,g95)
    c: Coincident(g95,g136)
    c: Coincident(g102,g135)
    c: Coincident(g102,g134)
    c: Coincident(g46,g133)
    c: Coincident(g46,g51)
FEATURE [Sketcher::SketchObject] Sketch003  label="2040-6"
  ArcFitTolerance = 1e-06
  FullyConstrained = false
  MakeInternals = false
  sketch-geometry (120):
    g0: LineSegment StartX=-12.9393 StartY=-4 StartZ=0 EndX=-10.6536 EndY=-4 EndZ=0
    g1: LineSegment StartX=-20 StartY=-3.3 StartZ=0 EndX=-20 EndY=-9 EndZ=0
    g2: LineSegment StartX=-13 StartY=-9.7 StartZ=0 EndX=-13 EndY=-8.3 EndZ=0
    g3: ArcOfCircle CenterX=-13.3 CenterY=-8.3 CenterZ=0 NormalX=0 NormalY=0 NormalZ=1 AngleXU=0 Radius=0.3 StartAngle=0 EndAngle=1.5708
    g4: LineSegment StartX=-19 StartY=-10 StartZ=0 EndX=-13.3 EndY=-10 EndZ=0
    g5: ArcOfCircle CenterX=-13.3 CenterY=-9.7 CenterZ=0 NormalX=0 NormalY=0 NormalZ=1 AngleXU=0 Radius=0.3 StartAngle=4.71239 EndAngle=6.28318
    g6: LineSegment StartX=-6.7 StartY=-10 StartZ=0 EndX=6.7 EndY=-10 EndZ=0
    g7: ArcOfCircle CenterX=-6.7 CenterY=-9.7 CenterZ=0 NormalX=0 NormalY=0 NormalZ=1 AngleXU=0 Radius=0.3 StartAngle=3.14159 EndAngle=4.71239
    g8: ArcOfCircle CenterX=6.7 CenterY=-9.7 CenterZ=0 NormalX=0 NormalY=0 NormalZ=1 AngleXU=0 Radius=0.3 StartAngle=4.71239 EndAngle=6.28318
    g9: LineSegment StartX=4 StartY=-8 StartZ=0 EndX=6.7 EndY=-8 EndZ=0
    g10: LineSegment StartX=7.06068 StartY=-4 StartZ=0 EndX=9.34641 EndY=-4 EndZ=0
    g11: LineSegment StartX=-1.7 StartY=-8 StartZ=0 EndX=1.7 EndY=-8 EndZ=0
    g12: ArcOfCircle CenterX=-1.7 CenterY=-7.7 CenterZ=0 NormalX=0 NormalY=0 NormalZ=1 AngleXU=0 Radius=0.3 StartAngle=3.14159 EndAngle=4.71239
    g13: ArcOfCircle CenterX=-19 CenterY=-9 CenterZ=0 NormalX=0 NormalY=0 NormalZ=1 AngleXU=0 Radius=1 StartAngle=3.14159 EndAngle=4.71239
    g14: LineSegment StartX=-16 StartY=-8 StartZ=0 EndX=-13.3 EndY=-8 EndZ=0
    g15: LineSegment StartX=-20 StartY=9 StartZ=0 EndX=-20 EndY=3.3 EndZ=0
    g16: LineSegment StartX=-13 StartY=9.7 StartZ=0 EndX=-13 EndY=8.3 EndZ=0
    g17: ArcOfCircle CenterX=-13.3 CenterY=8.3 CenterZ=0 NormalX=0 NormalY=0 NormalZ=1 AngleXU=0 Radius=0.3 StartAngle=4.71239 EndAngle=6.28318
    g18: ArcOfCircle CenterX=-13.3 CenterY=9.7 CenterZ=0 NormalX=0 NormalY=0 NormalZ=1 AngleXU=0 Radius=0.3 StartAngle=0 EndAngle=1.5708
    g19: LineSegment StartX=-16 StartY=-7.06066 StartZ=0 EndX=-12.9393 EndY=-4 EndZ=0
    g20: LineSegment StartX=-18 StartY=-6 StartZ=0 EndX=-18 EndY=-3.3 EndZ=0
    g21: ArcOfCircle CenterX=-18.3 CenterY=-3.3 CenterZ=0 NormalX=0 NormalY=0 NormalZ=1 AngleXU=0 Radius=0.3 StartAngle=0 EndAngle=1.5708
    g22: LineSegment StartX=-6 StartY=-2.93933 StartZ=0 EndX=-6 EndY=2.93934 EndZ=0
    g23: LineSegment StartX=-17.0607 StartY=-6 StartZ=0 EndX=-14 EndY=-2.93934 EndZ=0
    g24: LineSegment StartX=-18 StartY=-6 StartZ=0 EndX=-17.0607 EndY=-6 EndZ=0
    g25: LineSegment StartX=-16 StartY=-7.06066 StartZ=0 EndX=-16 EndY=-8 EndZ=0
    g26: LineSegment StartX=-19.7 StartY=-3 StartZ=0 EndX=-18.3 EndY=-3 EndZ=0
    g27: ArcOfCircle CenterX=-19.7 CenterY=-3.3 CenterZ=0 NormalX=0 NormalY=0 NormalZ=1 AngleXU=0 Radius=0.3 StartAngle=1.5708 EndAngle=3.14159
    g28: LineSegment StartX=-16 StartY=7.06064 StartZ=0 EndX=-12.9394 EndY=4 EndZ=0
    g29: LineSegment StartX=-17.0607 StartY=6 StartZ=0 EndX=-14 EndY=2.93932 EndZ=0
    g30: LineSegment StartX=-18 StartY=6 StartZ=0 EndX=-18 EndY=3.3 EndZ=0
    g31: LineSegment StartX=-14 StartY=2.93932 StartZ=0 EndX=-14 EndY=0.65359 EndZ=0
    g32: LineSegment StartX=-19.7 StartY=3 StartZ=0 EndX=-18.3 EndY=3 EndZ=0
    g33: ArcOfCircle CenterX=-18.3 CenterY=3.3 CenterZ=0 NormalX=0 NormalY=0 NormalZ=1 AngleXU=0 Radius=0.3 StartAngle=4.71239 EndAngle=6.28318
    g34: ArcOfCircle CenterX=-19.7 CenterY=3.3 CenterZ=0 NormalX=0 NormalY=0 NormalZ=1 AngleXU=0 Radius=0.3 StartAngle=3.14159 EndAngle=4.71239
    g35: LineSegment StartX=-18 StartY=6 StartZ=0 EndX=-17.0607 EndY=6 EndZ=0
    g36: LineSegment StartX=-16 StartY=8 StartZ=0 EndX=-13.3 EndY=8 EndZ=0
    g37: LineSegment StartX=-16 StartY=8 StartZ=0 EndX=-16 EndY=7.06064 EndZ=0
    g38: LineSegment StartX=-19 StartY=10 StartZ=0 EndX=-13.3 EndY=10 EndZ=0
    g39: LineSegment StartX=-6.7 StartY=10 StartZ=0 EndX=6.7 EndY=10 EndZ=0
    g40: ArcOfCircle CenterX=-6.7 CenterY=9.7 CenterZ=0 NormalX=0 NormalY=0 NormalZ=1 AngleXU=0 Radius=0.3 StartAngle=1.5708 EndAngle=3.14159
    g41: LineSegment StartX=-1.7 StartY=8 StartZ=0 EndX=1.7 EndY=8 EndZ=0
    g42: ArcOfCircle CenterX=-19 CenterY=9 CenterZ=0 NormalX=0 NormalY=0 NormalZ=1 AngleXU=0 Radius=1 StartAngle=1.5708 EndAngle=3.14159
    g43: LineSegment StartX=20 StartY=-3.3 StartZ=0 EndX=20 EndY=-9 EndZ=0
    g44: ArcOfCircle CenterX=19.7 CenterY=-3.3 CenterZ=0 NormalX=0 NormalY=0 NormalZ=1 AngleXU=0 Radius=0.3 StartAngle=0 EndAngle=1.5708
    g45: LineSegment StartX=18 StartY=-3.3 StartZ=0 EndX=18 EndY=-6 EndZ=0
    g46: LineSegment StartX=14 StartY=-0.653589 StartZ=0 EndX=14 EndY=-2.93935 EndZ=0
    g47: LineSegment StartX=6 StartY=2.93934 StartZ=0 EndX=6 EndY=-2.93934 EndZ=0
    g48: LineSegment StartX=13 StartY=-9.7 StartZ=0 EndX=13 EndY=-8.3 EndZ=0
    g49: LineSegment StartX=7 StartY=-9.7 StartZ=0 EndX=7 EndY=-8.3 EndZ=0
    g50: ArcOfCircle CenterX=6.7 CenterY=-8.3 CenterZ=0 NormalX=0 NormalY=0 NormalZ=1 AngleXU=0 Radius=0.3 StartAngle=0 EndAngle=1.5708
    g51: LineSegment StartX=-7 StartY=-9.7 StartZ=0 EndX=-7 EndY=-8.3 EndZ=0
    g52: ArcOfCircle CenterX=-6.7 CenterY=-8.3 CenterZ=0 NormalX=0 NormalY=0 NormalZ=1 AngleXU=0 Radius=0.3 StartAngle=1.5708 EndAngle=3.14159
    g53: LineSegment StartX=-6.7 StartY=-8 StartZ=0 EndX=-4 EndY=-8 EndZ=0
    g54: LineSegment StartX=19 StartY=-10 StartZ=0 EndX=13.3 EndY=-10 EndZ=0
    g55: ArcOfCircle CenterX=13.3 CenterY=-9.7 CenterZ=0 NormalX=0 NormalY=0 NormalZ=1 AngleXU=0 Radius=0.3 StartAngle=3.14159 EndAngle=4.71239
    g56: LineSegment StartX=16 StartY=-8 StartZ=0 EndX=13.3 EndY=-8 EndZ=0
    g57: ArcOfCircle CenterX=13.3 CenterY=-8.3 CenterZ=0 NormalX=0 NormalY=0 NormalZ=1 AngleXU=0 Radius=0.3 StartAngle=1.5708 EndAngle=3.14159
    g58: ArcOfCircle CenterX=19 CenterY=-9 CenterZ=0 NormalX=0 NormalY=0 NormalZ=1 AngleXU=0 Radius=1 StartAngle=4.71239 EndAngle=6.28318
    g59: LineSegment StartX=20 StartY=9 StartZ=0 EndX=20 EndY=3.3 EndZ=0
    g60: LineSegment StartX=13 StartY=9.7 StartZ=0 EndX=13 EndY=8.3 EndZ=0
    g61: ArcOfCircle CenterX=13.3 CenterY=9.7 CenterZ=0 NormalX=0 NormalY=0 NormalZ=1 AngleXU=0 Radius=0.3 StartAngle=1.5708 EndAngle=3.14159
    g62: LineSegment StartX=7 StartY=9.7 StartZ=0 EndX=7 EndY=8.3 EndZ=0
    g63: ArcOfCircle CenterX=6.7 CenterY=8.3 CenterZ=0 NormalX=0 NormalY=0 NormalZ=1 AngleXU=0 Radius=0.3 StartAngle=4.71239 EndAngle=6.28318
    g64: ArcOfCircle CenterX=6.7 CenterY=9.7 CenterZ=0 NormalX=0 NormalY=0 NormalZ=1 AngleXU=0 Radius=0.3 StartAngle=0 EndAngle=1.5708
    g65: LineSegment StartX=-7 StartY=9.7 StartZ=0 EndX=-7 EndY=8.3 EndZ=0
    g66: LineSegment StartX=4 StartY=8 StartZ=0 EndX=6.7 EndY=8 EndZ=0
    g67: LineSegment StartX=2.08787 StartY=-6.85147 StartZ=0 EndX=6 EndY=-2.93934 EndZ=0
    g68: LineSegment StartX=4 StartY=-7.06068 StartZ=0 EndX=7.06068 EndY=-4 EndZ=0
    g69: LineSegment StartX=4 StartY=7.06066 StartZ=0 EndX=7.06066 EndY=4 EndZ=0
    g70: LineSegment StartX=2.08787 StartY=6.85147 StartZ=0 EndX=6 EndY=2.93934 EndZ=0
    g71: Circle CenterX=-10 CenterY=0 CenterZ=0 NormalX=0 NormalY=0 NormalZ=-1 AngleXU=0 Radius=2.1
    g72: LineSegment StartX=-2.08786 StartY=-6.85148 StartZ=0 EndX=-6 EndY=-2.93933 EndZ=0
    g73: LineSegment StartX=-4 StartY=-7.06068 StartZ=0 EndX=-7.06068 EndY=-4 EndZ=0
    g74: LineSegment StartX=-4 StartY=-7.06068 StartZ=0 EndX=-4 EndY=-8 EndZ=0
    g75: LineSegment StartX=-2 StartY=-7.7 StartZ=0 EndX=-2 EndY=-7.0636 EndZ=0
    g76: LineSegment StartX=2 StartY=-7.7 StartZ=0 EndX=2 EndY=-7.0636 EndZ=0
    g77: ArcOfCircle CenterX=1.7 CenterY=-7.7 CenterZ=0 NormalX=0 NormalY=0 NormalZ=1 AngleXU=0 Radius=0.3 StartAngle=4.71239 EndAngle=6.28318
    g78: LineSegment StartX=4 StartY=-7.06068 StartZ=0 EndX=4 EndY=-8 EndZ=0
    g79: LineSegment StartX=-2.08786 StartY=6.85148 StartZ=0 EndX=-6 EndY=2.93934 EndZ=0
    g80: LineSegment StartX=-4 StartY=7.06066 StartZ=0 EndX=-7.06067 EndY=4 EndZ=0
    g81: LineSegment StartX=-4 StartY=8 StartZ=0 EndX=-6.7 EndY=8 EndZ=0
    g82: ArcOfCircle CenterX=-6.7 CenterY=8.3 CenterZ=0 NormalX=0 NormalY=0 NormalZ=1 AngleXU=0 Radius=0.3 StartAngle=3.14159 EndAngle=4.71239
    g83: LineSegment StartX=-7.06067 StartY=4 StartZ=0 EndX=-9.34641 EndY=4 EndZ=0
    g84: LineSegment StartX=-2 StartY=7.7 StartZ=0 EndX=-2 EndY=7.0636 EndZ=0
    g85: ArcOfCircle CenterX=-1.7 CenterY=7.7 CenterZ=0 NormalX=0 NormalY=0 NormalZ=1 AngleXU=0 Radius=0.3 StartAngle=1.5708 EndAngle=3.14159
    g86: LineSegment StartX=2 StartY=7.7 StartZ=0 EndX=2 EndY=7.0636 EndZ=0
    g87: ArcOfCircle CenterX=1.7 CenterY=7.7 CenterZ=0 NormalX=0 NormalY=0 NormalZ=1 AngleXU=0 Radius=0.3 StartAngle=0 EndAngle=1.5708
    g88: LineSegment StartX=4 StartY=8 StartZ=0 EndX=4 EndY=7.06066 EndZ=0
    g89: Circle CenterX=10 CenterY=0 CenterZ=0 NormalX=0 NormalY=0 NormalZ=-1 AngleXU=0 Radius=2.1
    g90: LineSegment StartX=16 StartY=-7.06066 StartZ=0 EndX=12.9393 EndY=-4 EndZ=0
    g91: LineSegment StartX=17.0607 StartY=-6 StartZ=0 EndX=14 EndY=-2.93935 EndZ=0
    g92: LineSegment StartX=16 StartY=-7.06066 StartZ=0 EndX=16 EndY=-8 EndZ=0
    g93: LineSegment StartX=18 StartY=-6 StartZ=0 EndX=17.0607 EndY=-6 EndZ=0
    g94: LineSegment StartX=19.7 StartY=-3 StartZ=0 EndX=18.3 EndY=-3 EndZ=0
    g95: ArcOfCircle CenterX=18.3 CenterY=-3.3 CenterZ=0 NormalX=0 NormalY=0 NormalZ=1 AngleXU=0 Radius=0.3 StartAngle=1.5708 EndAngle=3.14159
    g96: LineSegment StartX=16 StartY=8 StartZ=0 EndX=13.3 EndY=8 EndZ=0
    g97: ArcOfCircle CenterX=13.3 CenterY=8.3 CenterZ=0 NormalX=0 NormalY=0 NormalZ=1 AngleXU=0 Radius=0.3 StartAngle=3.14159 EndAngle=4.71239
    g98: LineSegment StartX=16 StartY=7.06064 StartZ=0 EndX=12.9394 EndY=4 EndZ=0
    g99: LineSegment StartX=17.0607 StartY=6 StartZ=0 EndX=14 EndY=2.93932 EndZ=0
    g100: LineSegment StartX=18 StartY=6 StartZ=0 EndX=18 EndY=3.3 EndZ=0
    g101: LineSegment StartX=19.7 StartY=3 StartZ=0 EndX=18.3 EndY=3 EndZ=0
    g102: ArcOfCircle CenterX=18.3 CenterY=3.3 CenterZ=0 NormalX=0 NormalY=0 NormalZ=1 AngleXU=0 Radius=0.3 StartAngle=3.14159 EndAngle=4.71239
    g103: ArcOfCircle CenterX=19.7 CenterY=3.3 CenterZ=0 NormalX=0 NormalY=0 NormalZ=1 AngleXU=0 Radius=0.3 StartAngle=4.71239 EndAngle=6.28318
    g104: LineSegment StartX=18 StartY=6 StartZ=0 EndX=17.0607 EndY=6 EndZ=0
    g105: LineSegment StartX=16 StartY=8 StartZ=0 EndX=16 EndY=7.06064 EndZ=0
    g106: LineSegment StartX=19 StartY=10 StartZ=0 EndX=13.3 EndY=10 EndZ=0
    g107: ArcOfCircle CenterX=19 CenterY=9 CenterZ=0 NormalX=0 NormalY=0 NormalZ=1 AngleXU=0 Radius=1 StartAngle=-5.33e-14 EndAngle=1.5708
    g108: LineSegment StartX=10.6536 StartY=4 StartZ=0 EndX=12.9394 EndY=4 EndZ=0
    g109: LineSegment StartX=-4 StartY=8 StartZ=0 EndX=-4 EndY=7.06066 EndZ=0
    g110: LineSegment StartX=-14 StartY=0.65359 StartZ=0 EndX=-14 EndY=-2.93934 EndZ=0
    g111: LineSegment StartX=-10.6536 StartY=-4 StartZ=0 EndX=-7.06068 EndY=-4 EndZ=0
    g112: LineSegment StartX=7.06066 StartY=4 StartZ=0 EndX=10.6536 EndY=4 EndZ=0
    g113: LineSegment StartX=14 StartY=2.93932 StartZ=0 EndX=14 EndY=-0.653589 EndZ=0
    g114: LineSegment StartX=9.34641 StartY=-4 StartZ=0 EndX=12.9393 EndY=-4 EndZ=0
    g115: LineSegment StartX=-12.9394 StartY=4 StartZ=0 EndX=-9.34641 EndY=4 EndZ=0
    g116: LineSegment StartX=-2.08786 StartY=6.85148 StartZ=0 EndX=-2 EndY=7.0636 EndZ=0
    g117: LineSegment StartX=2 StartY=7.0636 StartZ=0 EndX=2.08787 EndY=6.85147 EndZ=0
    g118: LineSegment StartX=-2.08786 StartY=-6.85148 StartZ=0 EndX=-2 EndY=-7.0636 EndZ=0
    g119: LineSegment StartX=2 StartY=-7.0636 StartZ=0 EndX=2.08787 EndY=-6.85147 EndZ=0
  constraints (124):
    c: Coincident(g110,g31)
    c: Coincident(g110,g23)
    c: Vertical(g110)
    c: Coincident(g111,g0)
    c: Coincident(g111,g73)
    c: Horizontal(g111)
    c: Coincident(g112,g69)
    c: Coincident(g112,g108)
    c: Horizontal(g112)
    c: Coincident(g113,g99)
    c: Coincident(g113,g46)
    c: Vertical(g113)
    c: Coincident(g114,g10)
    c: Coincident(g114,g90)
    c: Horizontal(g114)
    c: Coincident(g115,g28)
    c: Coincident(g115,g83)
    c: Horizontal(g115)
    c: Coincident(g116,g79)
    c: Coincident(g116,g84)
    c: Coincident(g117,g86)
    c: Coincident(g117,g70)
    c: Coincident(g118,g72)
    c: Coincident(g118,g75)
    c: Coincident(g119,g76)
    c: Coincident(g119,g67)
    c: Coincident(g1,g13)
    c: Coincident(g1,g27)
    c: Coincident(g15,g34)
    c: Coincident(g15,g42)
    c: Coincident(g26,g27)
    c: Coincident(g32,g34)
    c: Coincident(g4,g13)
    c: Coincident(g38,g42)
    c: Coincident(g21,g26)
    c: Coincident(g32,g33)
    c: Coincident(g20,g24)
    c: Coincident(g20,g21)
    c: Coincident(g30,g33)
    c: Coincident(g30,g35)
    c: Coincident(g23,g24)
    c: Coincident(g29,g35)
    c: Coincident(g14,g25)
    c: Coincident(g19,g25)
    c: Coincident(g28,g37)
    c: Coincident(g36,g37)
    c: Coincident(g29,g31)
    c: Coincident(g4,g5)
    c: Coincident(g3,g14)
    c: Coincident(g17,g36)
    c: Coincident(g18,g38)
    c: Coincident(g2,g5)
    c: Coincident(g2,g3)
    c: Coincident(g16,g17)
    c: Coincident(g16,g18)
    c: Coincident(g0,g19)
    c: Coincident(g80,g83)
    c: Coincident(g7,g51)
    c: Coincident(g51,g52)
    c: Coincident(g65,g82)
    c: Coincident(g40,g65)
    c: Coincident(g6,g7)
    c: Coincident(g52,g53)
    c: Coincident(g81,g82)
    c: Coincident(g39,g40)
    c: Coincident(g22,g72)
    c: Coincident(g22,g79)
    c: Coincident(g53,g74)
    c: Coincident(g73,g74)
    c: Coincident(g80,g109)
    c: Coincident(g81,g109)
    c: Coincident(g12,g75)
    c: Coincident(g84,g85)
    c: Coincident(g11,g12)
    c: Coincident(g41,g85)
    c: Coincident(g11,g77)
    c: Coincident(g41,g87)
    c: Coincident(g76,g77)
    c: Coincident(g86,g87)
    c: Coincident(g9,g78)
    c: Coincident(g68,g78)
    c: Coincident(g69,g88)
    c: Coincident(g66,g88)
    c: Coincident(g47,g67)
    c: Coincident(g47,g70)
    c: Coincident(g6,g8)
    c: Coincident(g9,g50)
    c: Coincident(g63,g66)
    c: Coincident(g39,g64)
    c: Coincident(g8,g49)
    c: Coincident(g49,g50)
    c: Coincident(g62,g63)
    c: Coincident(g62,g64)
    c: Coincident(g10,g68)
    c: Coincident(g98,g108)
    c: Coincident(g48,g55)
    c: Coincident(g48,g57)
    c: Coincident(g60,g97)
    c: Coincident(g60,g61)
    c: Coincident(g54,g55)
    c: Coincident(g56,g57)
    c: Coincident(g96,g97)
    c: Coincident(g61,g106)
    c: Coincident(g46,g91)
    c: Coincident(g56,g92)
    c: Coincident(g90,g92)
    c: Coincident(g98,g105)
    c: Coincident(g96,g105)
    c: Coincident(g91,g93)
    c: Coincident(g99,g104)
    c: Coincident(g45,g93)
    c: Coincident(g45,g95)
    c: Coincident(g100,g102)
    c: Coincident(g100,g104)
    c: Coincident(g94,g95)
    c: Coincident(g101,g102)
    c: Coincident(g54,g58)
    c: Coincident(g106,g107)
    c: Coincident(g44,g94)
    c: Coincident(g101,g103)
    c: Coincident(g43,g58)
    c: Coincident(g43,g44)
    c: Coincident(g59,g103)
    c: Coincident(g59,g107)
